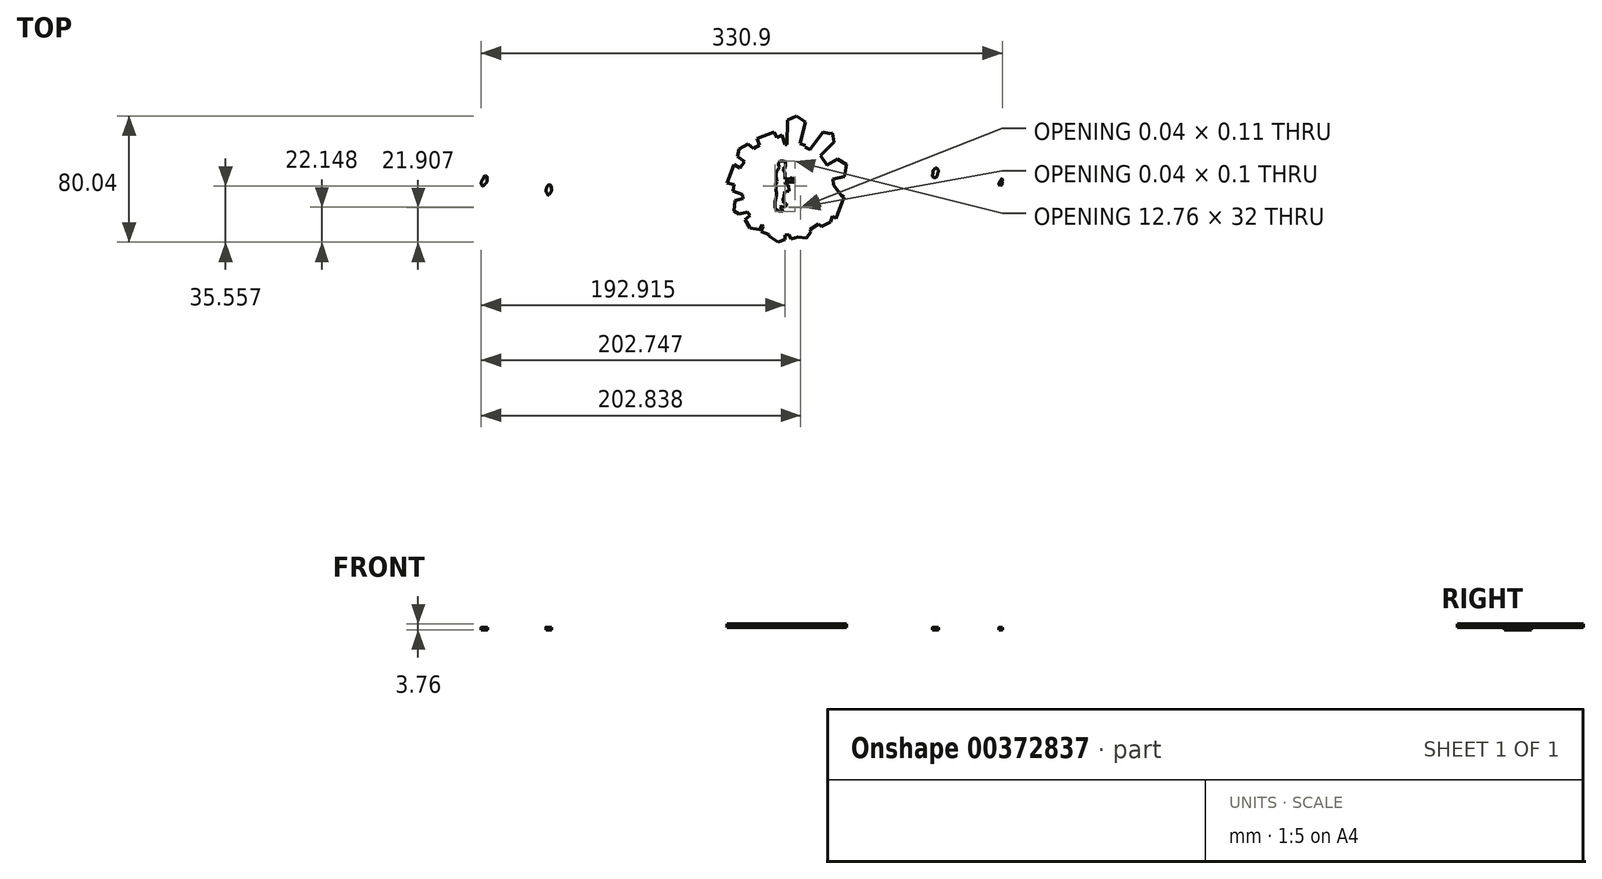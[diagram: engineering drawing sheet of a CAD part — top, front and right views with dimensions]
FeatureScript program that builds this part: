
annotation { "Feature Type Name" : "Feature", "Feature Type Description" : "" }
export const myFeature = defineFeature(function(context is Context, id is Id, definition is map)
    precondition{}
    {
        {
            var Q0;
            Q0=qCreatedBy(makeId("Top.planeOp"),FACE);
            var sketch = newSketch(context, id + "F0", { "sketchPlane" : qUnion([Q0])});
            skFitSpline(sketch, "E0", {"points": [v(-46.5, -16.11) * mm, v(-46.5, -16.11) * mm, v(-56.39, -13.57) * mm, v(-56.67, -12.44) * mm, v(-46.5, -16.11) * mm]});
            skFitSpline(sketch, "E1", {"points": [v(-56.67, -12.44) * mm, v(-56.95, -11.3) * mm, v(-55.82, -5.94) * mm, v(-55.82, -5.94) * mm, v(-56.67, -12.44) * mm]});
            skFitSpline(sketch, "E2", {"points": [v(-55.82, -5.94) * mm, v(-55.82, -5.94) * mm, v(-63.17, -5.09) * mm, v(-63.17, -3.96) * mm, v(-55.82, -5.94) * mm]});
            skFitSpline(sketch, "E3", {"points": [v(-63.17, -3.96) * mm, v(-63.17, -2.83) * mm, v(-55.54, 15.54) * mm, v(-55.54, 15.54) * mm, v(-63.17, -3.96) * mm]});
            skFitSpline(sketch, "E4", {"points": [v(21.34, -62.18) * mm, v(21.34, -62.18) * mm, v(14, -60.48) * mm, v(12.01, -61.33) * mm, v(21.34, -62.18) * mm]});
            skFitSpline(sketch, "E5", {"points": [v(12.01, -61.33) * mm, v(10.03, -62.18) * mm, v(4.66, -63.31) * mm, v(4.66, -63.31) * mm, v(12.01, -61.33) * mm]});
            skLineSegment(sketch, "E6", {"start": v(-55.54, 15.54) * mm, "end": v(-49.32, 11.59) * mm});
            skLineSegment(sketch, "E7", {"start": v(-49.32, 11.59) * mm, "end": v(-44.8, 18.37) * mm});
            skLineSegment(sketch, "E8", {"start": v(-44.8, 18.37) * mm, "end": v(-51.86, 23.74) * mm});
            skLineSegment(sketch, "E9", {"start": v(-51.86, 23.74) * mm, "end": v(-50.17, 31.66) * mm});
            skLineSegment(sketch, "E10", {"start": v(-50.17, 31.66) * mm, "end": v(-40.84, 37.03) * mm});
            skLineSegment(sketch, "E11", {"start": v(-40.84, 37.03) * mm, "end": v(-34.9, 32.5) * mm});
            skLineSegment(sketch, "E12", {"start": v(-34.9, 32.5) * mm, "end": v(-28.4, 36.18) * mm});
            skLineSegment(sketch, "E13", {"start": v(-28.4, 36.18) * mm, "end": v(-31.23, 42.68) * mm});
            skLineSegment(sketch, "E14", {"start": v(-31.23, 42.68) * mm, "end": v(-13.14, 49.74) * mm});
            skLineSegment(sketch, "E15", {"start": v(-13.14, 49.74) * mm, "end": v(-10.03, 43.8) * mm});
            skLineSegment(sketch, "E16", {"start": v(-10.03, 43.8) * mm, "end": v(-4.66, 46.63) * mm});
            skLineSegment(sketch, "E17", {"start": v(-4.66, 46.63) * mm, "end": v(-1.84, 36.74) * mm});
            skLineSegment(sketch, "E18", {"start": v(-1.84, 36.74) * mm, "end": v(0.42, 36.74) * mm});
            skLineSegment(sketch, "E19", {"start": v(0.42, 36.74) * mm, "end": v(0.99, 62.74) * mm});
            skLineSegment(sketch, "E20", {"start": v(0.99, 62.74) * mm, "end": v(10.32, 66.7) * mm});
            skLineSegment(sketch, "E21", {"start": v(10.32, 66.7) * mm, "end": v(20.2, 60.2) * mm});
            skLineSegment(sketch, "E22", {"start": v(20.2, 60.2) * mm, "end": v(14, 37.87) * mm});
            skLineSegment(sketch, "E23", {"start": v(14, 37.87) * mm, "end": v(20.2, 35.61) * mm});
            skLineSegment(sketch, "E24", {"start": v(20.2, 35.61) * mm, "end": v(19.64, 33.92) * mm});
            skLineSegment(sketch, "E25", {"start": v(19.64, 33.92) * mm, "end": v(25.01, 31.37) * mm});
            skLineSegment(sketch, "E26", {"start": v(25.01, 31.37) * mm, "end": v(38.3, 50.03) * mm});
            skLineSegment(sketch, "E27", {"start": v(38.3, 50.03) * mm, "end": v(45.36, 48.05) * mm});
            skLineSegment(sketch, "E28", {"start": v(45.36, 48.05) * mm, "end": v(48.75, 48.9) * mm});
            skLineSegment(sketch, "E29", {"start": v(48.75, 48.9) * mm, "end": v(50.17, 39.29) * mm});
            skLineSegment(sketch, "E30", {"start": v(50.17, 39.29) * mm, "end": v(35.75, 24.87) * mm});
            skLineSegment(sketch, "E31", {"start": v(35.75, 24.87) * mm, "end": v(42.82, 14.98) * mm});
            skLineSegment(sketch, "E32", {"start": v(42.82, 14.98) * mm, "end": v(53.84, 21.48) * mm});
            skLineSegment(sketch, "E33", {"start": v(53.84, 21.48) * mm, "end": v(63.17, 15.54) * mm});
            skLineSegment(sketch, "E34", {"start": v(63.17, 15.54) * mm, "end": v(61.47, 2.54) * mm});
            skLineSegment(sketch, "E35", {"start": v(61.47, 2.54) * mm, "end": v(49.32, 0) * mm});
            skLineSegment(sketch, "E36", {"start": v(49.32, 0) * mm, "end": v(49.89, -6.22) * mm});
            skLineSegment(sketch, "E37", {"start": v(49.89, -6.22) * mm, "end": v(58.36, -17.52) * mm});
            skLineSegment(sketch, "E38", {"start": v(58.36, -17.52) * mm, "end": v(60.9, -19.22) * mm});
            skLineSegment(sketch, "E39", {"start": v(60.9, -19.22) * mm, "end": v(52.15, -41.55) * mm});
            skLineSegment(sketch, "E40", {"start": v(52.15, -41.55) * mm, "end": v(48.47, -39.29) * mm});
            skLineSegment(sketch, "E41", {"start": v(48.47, -39.29) * mm, "end": v(46.5, -45.22) * mm});
            skLineSegment(sketch, "E42", {"start": v(46.5, -45.22) * mm, "end": v(36.88, -50.03) * mm});
            skLineSegment(sketch, "E43", {"start": v(36.88, -50.03) * mm, "end": v(33.77, -47.48) * mm});
            skLineSegment(sketch, "E44", {"start": v(33.77, -47.48) * mm, "end": v(24.73, -53.42) * mm});
            skLineSegment(sketch, "E45", {"start": v(24.73, -53.42) * mm, "end": v(25.58, -55.68) * mm});
            skLineSegment(sketch, "E46", {"start": v(25.58, -55.68) * mm, "end": v(21.34, -62.18) * mm});
            skFitSpline(sketch, "E47", {"points": [v(-7.41, 12.72) * mm, v(-7.66, 13.34) * mm, v(-8.77, 14.69) * mm, v(-8.77, 14.69) * mm, v(-7.41, 12.72) * mm]});
            skFitSpline(sketch, "E48", {"points": [v(-8.77, 14.69) * mm, v(-8.77, 14.69) * mm, v(-8.64, 16.16) * mm, v(-8.64, 16.9) * mm, v(-8.77, 14.69) * mm]});
            skFitSpline(sketch, "E49", {"points": [v(-8.64, 16.9) * mm, v(-8.64, 17.64) * mm, v(-6.8, 19.23) * mm, v(-6.8, 19.23) * mm, v(-8.64, 16.9) * mm]});
            skLineSegment(sketch, "E50", {"start": v(4.66, -63.31) * mm, "end": v(2.69, -58.79) * mm});
            skLineSegment(sketch, "E51", {"start": v(2.69, -58.79) * mm, "end": v(-1.84, -59.07) * mm});
            skLineSegment(sketch, "E52", {"start": v(-1.84, -59.07) * mm, "end": v(-1.84, -64.16) * mm});
            skLineSegment(sketch, "E53", {"start": v(-1.84, -64.16) * mm, "end": v(-9.19, -66.7) * mm});
            skLineSegment(sketch, "E54", {"start": v(-9.19, -66.7) * mm, "end": v(-18.8, -60.48) * mm});
            skLineSegment(sketch, "E55", {"start": v(-18.8, -60.48) * mm, "end": v(-18.51, -58.5) * mm});
            skLineSegment(sketch, "E56", {"start": v(-18.51, -58.5) * mm, "end": v(-27.27, -55.4) * mm});
            skLineSegment(sketch, "E57", {"start": v(-27.27, -55.4) * mm, "end": v(-24.73, -50.3) * mm});
            skLineSegment(sketch, "E58", {"start": v(-24.73, -50.3) * mm, "end": v(-26.14, -48.05) * mm});
            skLineSegment(sketch, "E59", {"start": v(-26.14, -48.05) * mm, "end": v(-28.69, -53.14) * mm});
            skLineSegment(sketch, "E60", {"start": v(-28.69, -53.14) * mm, "end": v(-38.86, -51.72) * mm});
            skLineSegment(sketch, "E61", {"start": v(-38.86, -51.72) * mm, "end": v(-44.23, -42.68) * mm});
            skLineSegment(sketch, "E62", {"start": v(-44.23, -42.68) * mm, "end": v(-38.58, -38.72) * mm});
            skLineSegment(sketch, "E63", {"start": v(-38.58, -38.72) * mm, "end": v(-41.12, -35.05) * mm});
            skLineSegment(sketch, "E64", {"start": v(-41.12, -35.05) * mm, "end": v(-50.45, -37.03) * mm});
            skLineSegment(sketch, "E65", {"start": v(-50.45, -37.03) * mm, "end": v(-55.54, -33.63) * mm});
            skLineSegment(sketch, "E66", {"start": v(-55.54, -33.63) * mm, "end": v(-54.4, -22.61) * mm});
            skLineSegment(sketch, "E67", {"start": v(-54.4, -22.61) * mm, "end": v(-45.93, -20.63) * mm});
            skLineSegment(sketch, "E68", {"start": v(-45.93, -20.63) * mm, "end": v(-46.5, -16.11) * mm});
            skFitSpline(sketch, "E69", {"points": [v(-1.02, 13.95) * mm, v(-1.02, 13.95) * mm, v(-1.76, 13.34) * mm, v(-1.88, 12.6) * mm, v(-1.02, 13.95) * mm]});
            skFitSpline(sketch, "E70", {"points": [v(-1.88, 12.6) * mm, v(-2, 11.86) * mm, v(-1.88, 11.12) * mm, v(-1.88, 11.12) * mm, v(-1.88, 12.6) * mm]});
            skLineSegment(sketch, "E71", {"start": v(-6.8, 19.23) * mm, "end": v(-3.6, 19.11) * mm});
            skLineSegment(sketch, "E72", {"start": v(-3.6, 19.11) * mm, "end": v(-1.27, 18.62) * mm});
            skLineSegment(sketch, "E73", {"start": v(-1.27, 18.62) * mm, "end": v(-1.4, 16.16) * mm});
            skLineSegment(sketch, "E74", {"start": v(-1.4, 16.16) * mm, "end": v(-1.02, 13.95) * mm});
            skFitSpline(sketch, "E75", {"points": [v(-1.76, 6.58) * mm, v(-1.76, 6.58) * mm, v(-2, 4.36) * mm, v(-1.88, 3.87) * mm, v(-1.76, 6.58) * mm]});
            skFitSpline(sketch, "E76", {"points": [v(-1.88, 3.87) * mm, v(-1.76, 3.38) * mm, v(-1.52, 0.3) * mm, v(-1.52, 0.3) * mm, v(-1.88, 3.87) * mm]});
            skLineSegment(sketch, "E77", {"start": v(-1.88, 11.12) * mm, "end": v(-3.36, 11.37) * mm});
            skLineSegment(sketch, "E78", {"start": v(-3.36, 11.37) * mm, "end": v(-4.34, 10.88) * mm});
            skLineSegment(sketch, "E79", {"start": v(-4.34, 10.88) * mm, "end": v(-3.36, 9.4) * mm});
            skLineSegment(sketch, "E80", {"start": v(-3.36, 9.4) * mm, "end": v(-2.5, 8.54) * mm});
            skLineSegment(sketch, "E81", {"start": v(-2.5, 8.54) * mm, "end": v(-1.76, 6.58) * mm});
            skFitSpline(sketch, "E82", {"points": [v(5.74, 2.28) * mm, v(5.74, 2.28) * mm, v(6.84, 1.3) * mm, v(6.47, 0.92) * mm, v(5.74, 2.28) * mm]});
            skFitSpline(sketch, "E83", {"points": [v(6.47, 0.92) * mm, v(6.1, 0.55) * mm, v(5.24, -0.06) * mm, v(5.24, -0.06) * mm, v(6.47, 0.92) * mm]});
            skLineSegment(sketch, "E84", {"start": v(-1.52, 0.3) * mm, "end": v(3.03, -0.06) * mm});
            skLineSegment(sketch, "E85", {"start": v(3.03, -0.06) * mm, "end": v(5.37, 1.54) * mm});
            skLineSegment(sketch, "E86", {"start": v(5.37, 1.54) * mm, "end": v(5.74, 2.28) * mm});
            skFitSpline(sketch, "E87", {"points": [v(-4.46, -34.1) * mm, v(-4.46, -34.1) * mm, v(-6.92, -33.98) * mm, v(-7.54, -33.85) * mm, v(-4.46, -34.1) * mm]});
            skFitSpline(sketch, "E88", {"points": [v(-7.54, -33.85) * mm, v(-8.15, -33.73) * mm, v(-9.5, -33.24) * mm, v(-10, -33) * mm]});
            skFitSpline(sketch, "E89", {"points": [v(-10, -33) * mm, v(-10.49, -32.75) * mm, v(-12.33, -30.66) * mm, v(-12.33, -30.66) * mm, v(-10, -33) * mm]});
            skLineSegment(sketch, "E90", {"start": v(5.24, -0.06) * mm, "end": v(7.58, -0.67) * mm});
            skLineSegment(sketch, "E91", {"start": v(7.58, -0.67) * mm, "end": v(8.93, -1.9) * mm});
            skLineSegment(sketch, "E92", {"start": v(8.93, -1.9) * mm, "end": v(7.82, -2.89) * mm});
            skLineSegment(sketch, "E93", {"start": v(7.82, -2.89) * mm, "end": v(2.3, -3.13) * mm});
            skLineSegment(sketch, "E94", {"start": v(2.3, -3.13) * mm, "end": v(-1.64, -2.89) * mm});
            skLineSegment(sketch, "E95", {"start": v(-1.64, -2.89) * mm, "end": v(-1.27, -5.22) * mm});
            skLineSegment(sketch, "E96", {"start": v(-1.27, -5.22) * mm, "end": v(-0.04, -6.45) * mm});
            skLineSegment(sketch, "E97", {"start": v(-0.04, -6.45) * mm, "end": v(2.17, -6.2) * mm});
            skLineSegment(sketch, "E98", {"start": v(2.17, -6.2) * mm, "end": v(2.42, -12.72) * mm});
            skLineSegment(sketch, "E99", {"start": v(2.42, -12.72) * mm, "end": v(-2, -12.96) * mm});
            skLineSegment(sketch, "E100", {"start": v(-2, -12.96) * mm, "end": v(-2.74, -18.98) * mm});
            skLineSegment(sketch, "E101", {"start": v(-2.74, -18.98) * mm, "end": v(-3.6, -21.32) * mm});
            skLineSegment(sketch, "E102", {"start": v(-3.6, -21.32) * mm, "end": v(-3.36, -25.37) * mm});
            skLineSegment(sketch, "E103", {"start": v(-3.36, -25.37) * mm, "end": v(-0.16, -26.11) * mm});
            skLineSegment(sketch, "E104", {"start": v(-0.16, -26.11) * mm, "end": v(0.08, -28.2) * mm});
            skLineSegment(sketch, "E105", {"start": v(0.08, -28.2) * mm, "end": v(-2, -29.43) * mm});
            skLineSegment(sketch, "E106", {"start": v(-2, -29.43) * mm, "end": v(-5.57, -29.3) * mm});
            skLineSegment(sketch, "E107", {"start": v(-5.57, -29.3) * mm, "end": v(-6.92, -29.68) * mm});
            skLineSegment(sketch, "E108", {"start": v(-6.92, -29.68) * mm, "end": v(-4.96, -31.89) * mm});
            skLineSegment(sketch, "E109", {"start": v(-4.96, -31.89) * mm, "end": v(-4.46, -34.1) * mm});
            skFitSpline(sketch, "E110", {"points": [v(-12.33, -24.15) * mm, v(-12.33, -24.15) * mm, v(-11.22, -20.1) * mm, v(-11.1, -19.35) * mm, v(-12.33, -24.15) * mm]});
            skFitSpline(sketch, "E111", {"points": [v(-11.1, -19.35) * mm, v(-10.98, -18.62) * mm, v(-10.6, -15.05) * mm, v(-10.73, -14.44) * mm]});
            skFitSpline(sketch, "E112", {"points": [v(-10.73, -14.44) * mm, v(-10.85, -13.82) * mm, v(-11.22, -10.87) * mm, v(-11.35, -10.14) * mm]});
            skFitSpline(sketch, "E113", {"points": [v(-11.35, -10.14) * mm, v(-11.47, -9.4) * mm, v(-11.47, -5.34) * mm, v(-11.47, -5.34) * mm, v(-11.35, -10.14) * mm]});
            skFitSpline(sketch, "E114", {"points": [v(-11.47, -5.34) * mm, v(-11.47, -5.34) * mm, v(-10.49, -3.13) * mm, v(-10.36, -2.64) * mm, v(-11.47, -5.34) * mm]});
            skFitSpline(sketch, "E115", {"points": [v(-10.36, -2.64) * mm, v(-10.24, -2.15) * mm, v(-10.6, -0.06) * mm, v(-10.6, -0.06) * mm, v(-10.36, -2.64) * mm]});
            skFitSpline(sketch, "E116", {"points": [v(-10.6, -0.06) * mm, v(-10.6, -0.06) * mm, v(-11.3, 3.5) * mm, v(-11.22, 4.12) * mm, v(-10.6, -0.06) * mm]});
            skLineSegment(sketch, "E117", {"start": v(-12.33, -30.66) * mm, "end": v(-12.33, -24.15) * mm});
            skLineSegment(sketch, "E118", {"start": v(-12.33, -24.15) * mm, "end": v(-12.33, -30.66) * mm});
            skLineSegment(sketch, "E119", {"start": v(-11.22, 4.12) * mm, "end": v(-10.73, 8.17) * mm});
            skLineSegment(sketch, "E120", {"start": v(-10.73, 8.17) * mm, "end": v(-9.26, 9.9) * mm});
            skLineSegment(sketch, "E121", {"start": v(-9.26, 9.9) * mm, "end": v(-8.4, 11.25) * mm});
            skLineSegment(sketch, "E122", {"start": v(-8.4, 11.25) * mm, "end": v(-7.41, 12.72) * mm});
            skFitSpline(sketch, "E123", {"points": [v(19.38, 11.86) * mm, v(19.38, 11.86) * mm, v(19.25, 12.72) * mm, v(19.25, 13.21) * mm, v(19.38, 11.86) * mm]});
            skFitSpline(sketch, "E124", {"points": [v(19.25, 13.21) * mm, v(19.25, 13.7) * mm, v(19.25, 14.32) * mm, v(19.13, 14.8) * mm]});
            skFitSpline(sketch, "E125", {"points": [v(19.13, 14.8) * mm, v(19, 15.3) * mm, v(18.64, 15.42) * mm, v(18.64, 16.04) * mm]});
            skFitSpline(sketch, "E126", {"points": [v(18.64, 16.04) * mm, v(18.64, 16.65) * mm, v(20.48, 17.76) * mm, v(20.48, 17.76) * mm, v(18.64, 16.04) * mm]});
            skLineSegment(sketch, "E127", {"start": v(22.08, 9.03) * mm, "end": v(20.36, 10.63) * mm});
            skLineSegment(sketch, "E128", {"start": v(20.36, 10.63) * mm, "end": v(19.38, 11.86) * mm});
            skFitSpline(sketch, "E129", {"points": [v(23.06, 18.62) * mm, v(23.06, 18.62) * mm, v(24.05, 18.13) * mm, v(24.41, 18.13) * mm, v(23.06, 18.62) * mm]});
            skFitSpline(sketch, "E130", {"points": [v(24.41, 18.13) * mm, v(24.78, 18.13) * mm, v(25.52, 17.27) * mm, v(25.52, 17.27) * mm, v(24.41, 18.13) * mm]});
            skLineSegment(sketch, "E131", {"start": v(20.48, 17.76) * mm, "end": v(21.34, 18.37) * mm});
            skLineSegment(sketch, "E132", {"start": v(21.34, 18.37) * mm, "end": v(23.06, 18.62) * mm});
            skFitSpline(sketch, "E133", {"points": [v(26.01, 16.28) * mm, v(26.01, 16.28) * mm, v(25.89, 15.92) * mm, v(25.89, 15.3) * mm, v(26.01, 16.28) * mm]});
            skLineSegment(sketch, "E134", {"start": v(25.52, 17.27) * mm, "end": v(26.01, 16.28) * mm});
            skFitSpline(sketch, "E135", {"points": [v(28.35, 9.53) * mm, v(28.35, 9.53) * mm, v(28.84, 8.91) * mm, v(29.2, 8.42) * mm, v(28.35, 9.53) * mm]});
            skFitSpline(sketch, "E136", {"points": [v(29.2, 8.42) * mm, v(29.58, 7.93) * mm, v(30.19, 8.17) * mm, v(30.19, 7.2) * mm]});
            skFitSpline(sketch, "E137", {"points": [v(30.19, 7.2) * mm, v(30.19, 6.2) * mm, v(29.94, 5.22) * mm, v(29.94, 4.49) * mm]});
            skFitSpline(sketch, "E138", {"points": [v(29.94, 4.49) * mm, v(29.94, 3.75) * mm, v(30.19, 3.01) * mm, v(30.19, 2.4) * mm]});
            skFitSpline(sketch, "E139", {"points": [v(30.19, 2.4) * mm, v(30.19, 1.78) * mm, v(29.45, 0.06) * mm, v(29.7, -1.04) * mm]});
            skFitSpline(sketch, "E140", {"points": [v(29.7, -1.04) * mm, v(29.94, -2.15) * mm, v(29.94, -2.4) * mm, v(30.07, -2.76) * mm]});
            skFitSpline(sketch, "E141", {"points": [v(30.07, -2.76) * mm, v(30.19, -3.13) * mm, v(30.56, -4.6) * mm, v(30.56, -5.1) * mm]});
            skFitSpline(sketch, "E142", {"points": [v(30.56, -5.1) * mm, v(30.56, -5.59) * mm, v(30.44, -6.57) * mm, v(29.82, -7.43) * mm]});
            skFitSpline(sketch, "E143", {"points": [v(29.82, -7.43) * mm, v(29.2, -8.3) * mm, v(29.08, -7.8) * mm, v(29.08, -8.54) * mm]});
            skFitSpline(sketch, "E144", {"points": [v(29.08, -8.54) * mm, v(29.08, -9.28) * mm, v(28.96, -8.78) * mm, v(29.08, -9.77) * mm]});
            skFitSpline(sketch, "E145", {"points": [v(29.08, -9.77) * mm, v(29.2, -10.75) * mm, v(29.2, -11.12) * mm, v(29.2, -11.73) * mm]});
            skFitSpline(sketch, "E146", {"points": [v(29.2, -11.73) * mm, v(29.2, -12.35) * mm, v(29.33, -13.7) * mm, v(29.33, -13.7) * mm, v(29.2, -11.73) * mm]});
            skLineSegment(sketch, "E147", {"start": v(25.89, 15.3) * mm, "end": v(25.89, 13.95) * mm});
            skLineSegment(sketch, "E148", {"start": v(25.89, 13.95) * mm, "end": v(25.64, 13.21) * mm});
            skLineSegment(sketch, "E149", {"start": v(25.64, 13.21) * mm, "end": v(25.52, 12.23) * mm});
            skLineSegment(sketch, "E150", {"start": v(25.52, 12.23) * mm, "end": v(26.01, 11.25) * mm});
            skLineSegment(sketch, "E151", {"start": v(26.01, 11.25) * mm, "end": v(28.35, 9.53) * mm});
            skFitSpline(sketch, "E152", {"points": [v(23.8, -35.33) * mm, v(23.8, -35.33) * mm, v(23.19, -35.08) * mm, v(22.7, -35.08) * mm, v(23.8, -35.33) * mm]});
            skFitSpline(sketch, "E153", {"points": [v(22.7, -35.08) * mm, v(22.2, -35.08) * mm, v(21.71, -34.84) * mm, v(21.71, -34.84) * mm, v(22.7, -35.08) * mm]});
            skLineSegment(sketch, "E154", {"start": v(29.33, -13.7) * mm, "end": v(34.61, -13.7) * mm});
            skLineSegment(sketch, "E155", {"start": v(34.61, -13.7) * mm, "end": v(35.1, -24.27) * mm});
            skLineSegment(sketch, "E156", {"start": v(35.1, -24.27) * mm, "end": v(28.96, -25.13) * mm});
            skLineSegment(sketch, "E157", {"start": v(28.96, -25.13) * mm, "end": v(29.33, -28.82) * mm});
            skLineSegment(sketch, "E158", {"start": v(29.33, -28.82) * mm, "end": v(29.33, -31.64) * mm});
            skLineSegment(sketch, "E159", {"start": v(29.33, -31.64) * mm, "end": v(29.33, -33.49) * mm});
            skLineSegment(sketch, "E160", {"start": v(29.33, -33.49) * mm, "end": v(27.13, -34.53) * mm});
            skLineSegment(sketch, "E161", {"start": v(27.13, -34.53) * mm, "end": v(25.52, -35.2) * mm});
            skLineSegment(sketch, "E162", {"start": v(25.52, -35.2) * mm, "end": v(23.8, -35.33) * mm});
            skFitSpline(sketch, "E163", {"points": [v(21.71, -34.22) * mm, v(21.71, -34.22) * mm, v(21.34, -34.35) * mm, v(21.83, -33.73) * mm, v(21.71, -34.22) * mm]});
            skFitSpline(sketch, "E164", {"points": [v(21.83, -33.73) * mm, v(22.32, -33.12) * mm, v(22.45, -33.12) * mm, v(22.45, -33.12) * mm, v(21.83, -33.73) * mm]});
            skLineSegment(sketch, "E165", {"start": v(21.71, -34.84) * mm, "end": v(21.71, -34.22) * mm});
            skFitSpline(sketch, "E166", {"points": [v(24.3, -32.26) * mm, v(24.66, -32.01) * mm, v(24.78, -31.76) * mm, v(24.78, -31.76) * mm, v(24.3, -32.26) * mm]});
            skLineSegment(sketch, "E167", {"start": v(22.45, -33.12) * mm, "end": v(23.92, -32.5) * mm});
            skLineSegment(sketch, "E168", {"start": v(23.92, -32.5) * mm, "end": v(24.3, -32.26) * mm});
            skFitSpline(sketch, "E169", {"points": [v(24.3, -29.92) * mm, v(24.3, -29.92) * mm, v(24.41, -30.29) * mm, v(24.17, -29.8) * mm, v(24.3, -29.92) * mm]});
            skFitSpline(sketch, "E170", {"points": [v(24.17, -29.8) * mm, v(23.92, -29.3) * mm, v(23.68, -28.57) * mm, v(23.68, -28.57) * mm, v(24.17, -29.8) * mm]});
            skFitSpline(sketch, "E171", {"points": [v(23.68, -28.57) * mm, v(23.68, -28.57) * mm, v(23.55, -28.57) * mm, v(23.43, -29.18) * mm, v(23.68, -28.57) * mm]});
            skFitSpline(sketch, "E172", {"points": [v(23.43, -29.18) * mm, v(23.3, -29.8) * mm, v(22.7, -30.84) * mm, v(22.7, -30.84) * mm, v(23.43, -29.18) * mm]});
            skLineSegment(sketch, "E173", {"start": v(24.78, -31.76) * mm, "end": v(24.78, -31.03) * mm});
            skLineSegment(sketch, "E174", {"start": v(24.78, -31.03) * mm, "end": v(24.3, -29.92) * mm});
            skFitSpline(sketch, "E175", {"points": [v(22.94, -30.66) * mm, v(22.94, -30.66) * mm, v(22.45, -30.84) * mm, v(21.83, -30.72) * mm, v(22.94, -30.66) * mm]});
            skFitSpline(sketch, "E176", {"points": [v(21.83, -30.72) * mm, v(21.22, -30.6) * mm, v(21.59, -30.72) * mm, v(20.85, -30.6) * mm]});
            skFitSpline(sketch, "E177", {"points": [v(20.85, -30.6) * mm, v(20.11, -30.47) * mm, v(21.1, -30.47) * mm, v(20, -30.47) * mm]});
            skFitSpline(sketch, "E178", {"points": [v(20, -30.47) * mm, v(18.88, -30.47) * mm, v(19.87, -30.35) * mm, v(18.88, -30.47) * mm]});
            skFitSpline(sketch, "E179", {"points": [v(18.88, -30.47) * mm, v(17.9, -30.6) * mm, v(17.78, -30.6) * mm, v(17.78, -30.6) * mm, v(18.88, -30.47) * mm]});
            skFitSpline(sketch, "E180", {"points": [v(17.78, -30.6) * mm, v(17.78, -30.6) * mm, v(17.78, -30.72) * mm, v(17.04, -30.47) * mm, v(17.78, -30.6) * mm]});
            skFitSpline(sketch, "E181", {"points": [v(17.04, -30.47) * mm, v(16.3, -30.23) * mm, v(16.92, -30.66) * mm, v(15.93, -30.54) * mm]});
            skFitSpline(sketch, "E182", {"points": [v(15.93, -30.54) * mm, v(14.95, -30.41) * mm, v(15.2, -30.23) * mm, v(14.7, -29.86) * mm]});
            skFitSpline(sketch, "E183", {"points": [v(14.7, -29.86) * mm, v(14.66, -29.7) * mm, v(14.87, -30.27) * mm, v(14.83, -30.1) * mm]});
            skFitSpline(sketch, "E184", {"points": [v(14.83, -30.1) * mm, v(12.95, -28.8) * mm, v(16.5, -27.6) * mm, v(17.35, -27.34) * mm]});
            skFitSpline(sketch, "E185", {"points": [v(17.35, -27.34) * mm, v(18.95, -26.85) * mm, v(19.25, -26.91) * mm, v(19.25, -26.91) * mm, v(17.35, -27.34) * mm]});
            skLineSegment(sketch, "E186", {"start": v(22.7, -30.84) * mm, "end": v(22.94, -30.66) * mm});
            skFitSpline(sketch, "E187", {"points": [v(20.11, -11.98) * mm, v(20.11, -11) * mm, v(20.24, -10.26) * mm, v(20, -9.52) * mm]});
            skFitSpline(sketch, "E188", {"points": [v(20, -9.52) * mm, v(19.74, -8.78) * mm, v(19.5, -7.92) * mm, v(19.87, -6.82) * mm]});
            skFitSpline(sketch, "E189", {"points": [v(19.87, -6.82) * mm, v(20.24, -5.71) * mm, v(20.11, -2.89) * mm, v(20.11, -2.89) * mm, v(19.87, -6.82) * mm]});
            skLineSegment(sketch, "E190", {"start": v(19.25, -26.91) * mm, "end": v(20, -26.3) * mm});
            skLineSegment(sketch, "E191", {"start": v(20, -26.3) * mm, "end": v(20.24, -24.51) * mm});
            skLineSegment(sketch, "E192", {"start": v(20.24, -24.51) * mm, "end": v(20.11, -18.25) * mm});
            skLineSegment(sketch, "E193", {"start": v(20.11, -18.25) * mm, "end": v(20.11, -15.05) * mm});
            skLineSegment(sketch, "E194", {"start": v(20.11, -15.05) * mm, "end": v(20.11, -11.98) * mm});
            skFitSpline(sketch, "E195", {"points": [v(19.38, -1.78) * mm, v(19.38, -1.78) * mm, v(18.64, -2.4) * mm, v(17.4, -3.13) * mm, v(19.38, -1.78) * mm]});
            skFitSpline(sketch, "E196", {"points": [v(17.4, -3.13) * mm, v(16.18, -3.87) * mm, v(15.57, -4.11) * mm, v(15.57, -4.11) * mm, v(17.4, -3.13) * mm]});
            skLineSegment(sketch, "E197", {"start": v(20.11, -2.89) * mm, "end": v(19.38, -1.78) * mm});
            skFitSpline(sketch, "E198", {"points": [v(15.07, -3.62) * mm, v(15.07, -3.62) * mm, v(15.57, -3.38) * mm, v(14.46, -3.38) * mm, v(15.07, -3.62) * mm]});
            skLineSegment(sketch, "E199", {"start": v(15.57, -4.11) * mm, "end": v(15.07, -3.62) * mm});
            skLineSegment(sketch, "E200", {"start": v(14.46, -3.38) * mm, "end": v(12.99, -3.38) * mm});
            skLineSegment(sketch, "E201", {"start": v(12.99, -3.38) * mm, "end": v(11.51, -3.38) * mm});
            skLineSegment(sketch, "E202", {"start": v(11.51, -3.38) * mm, "end": v(10.53, -2.89) * mm});
            skLineSegment(sketch, "E203", {"start": v(10.53, -2.89) * mm, "end": v(12, -1.66) * mm});
            skLineSegment(sketch, "E204", {"start": v(12, -1.66) * mm, "end": v(12.62, -1.17) * mm});
            skLineSegment(sketch, "E205", {"start": v(12.62, -1.17) * mm, "end": v(12.99, -0.92) * mm});
            skLineSegment(sketch, "E206", {"start": v(12.99, -0.92) * mm, "end": v(12.62, 0.19) * mm});
            skLineSegment(sketch, "E207", {"start": v(12.62, 0.19) * mm, "end": v(13.1, 0.55) * mm});
            skLineSegment(sketch, "E208", {"start": v(13.1, 0.55) * mm, "end": v(13.6, 0.55) * mm});
            skFitSpline(sketch, "E209", {"points": [v(20.6, 7.31) * mm, v(20.6, 7.31) * mm, v(20.24, 6.33) * mm, v(20.24, 5.72) * mm, v(20.6, 7.31) * mm]});
            skFitSpline(sketch, "E210", {"points": [v(20.24, 5.72) * mm, v(20.24, 5.1) * mm, v(20.11, 4) * mm, v(20.11, 4) * mm, v(20.24, 5.72) * mm]});
            skLineSegment(sketch, "E211", {"start": v(21.96, 9.53) * mm, "end": v(20.6, 7.31) * mm});
            skLineSegment(sketch, "E212", {"start": v(20.11, 4) * mm, "end": v(19.74, 1.9) * mm});
            skLineSegment(sketch, "E213", {"start": v(19.74, 1.9) * mm, "end": v(19.25, 1.42) * mm});
            skLineSegment(sketch, "E214", {"start": v(19.25, 1.42) * mm, "end": v(17.78, 0.43) * mm});
            skLineSegment(sketch, "E215", {"start": v(17.78, 0.43) * mm, "end": v(15.32, -0.3) * mm});
            skLineSegment(sketch, "E216", {"start": v(15.32, -0.3) * mm, "end": v(13.35, 0.43) * mm});
            skLineSegment(sketch, "E217", {"start": v(13.35, 0.43) * mm, "end": v(13.1, 0.55) * mm});
            skSolve(sketch);
        }
        {
            var Q0;
            Q0=qCreatedBy(makeId("Top.planeOp"),FACE);
            var sketch = newSketch(context, id + "F1", { "sketchPlane" : qUnion([Q0])});
            skLineSegment(sketch, "E218.0.0", {"start": v(20.36, 10.63) * mm, "end": v(21.8, 9.28) * mm});
            skLineSegment(sketch, "E218.0.1", {"start": v(21.8, 9.28) * mm, "end": v(20.6, 7.31) * mm});
            skLineSegment(sketch, "E218.0.2", {"start": v(20.6, 7.31) * mm, "end": v(20.24, 5.72) * mm});
            skLineSegment(sketch, "E218.0.3", {"start": v(20.24, 5.72) * mm, "end": v(20.11, 4) * mm});
            skLineSegment(sketch, "E218.0.4", {"start": v(20.11, 4) * mm, "end": v(19.74, 1.9) * mm});
            skLineSegment(sketch, "E218.0.5", {"start": v(19.74, 1.9) * mm, "end": v(19.25, 1.42) * mm});
            skLineSegment(sketch, "E218.0.6", {"start": v(19.25, 1.42) * mm, "end": v(17.78, 0.43) * mm});
            skLineSegment(sketch, "E218.0.7", {"start": v(17.78, 0.43) * mm, "end": v(15.32, -0.3) * mm});
            skLineSegment(sketch, "E218.0.8", {"start": v(15.32, -0.3) * mm, "end": v(13.35, 0.43) * mm});
            skLineSegment(sketch, "E218.0.9", {"start": v(13.35, 0.43) * mm, "end": v(13.1, 0.55) * mm});
            skLineSegment(sketch, "E218.0.10", {"start": v(13.1, 0.55) * mm, "end": v(12.62, 0.19) * mm});
            skLineSegment(sketch, "E218.0.11", {"start": v(12.62, 0.19) * mm, "end": v(12.99, -0.92) * mm});
            skLineSegment(sketch, "E218.0.12", {"start": v(12.99, -0.92) * mm, "end": v(12.62, -1.17) * mm});
            skLineSegment(sketch, "E218.0.13", {"start": v(12.62, -1.17) * mm, "end": v(12, -1.66) * mm});
            skLineSegment(sketch, "E218.0.14", {"start": v(12, -1.66) * mm, "end": v(10.53, -2.89) * mm});
            skLineSegment(sketch, "E218.0.15", {"start": v(10.53, -2.89) * mm, "end": v(11.51, -3.38) * mm});
            skLineSegment(sketch, "E218.0.16", {"start": v(11.51, -3.38) * mm, "end": v(12.99, -3.38) * mm});
            skLineSegment(sketch, "E218.0.17", {"start": v(12.99, -3.38) * mm, "end": v(14.46, -3.38) * mm});
            skLineSegment(sketch, "E218.0.18", {"start": v(14.46, -3.38) * mm, "end": v(15.07, -3.62) * mm});
            skLineSegment(sketch, "E218.0.19", {"start": v(15.07, -3.62) * mm, "end": v(15.57, -4.11) * mm});
            skLineSegment(sketch, "E218.0.20", {"start": v(15.57, -4.11) * mm, "end": v(17.4, -3.13) * mm});
            skLineSegment(sketch, "E218.0.21", {"start": v(17.4, -3.13) * mm, "end": v(19.38, -1.78) * mm});
            skLineSegment(sketch, "E218.0.22", {"start": v(19.38, -1.78) * mm, "end": v(20.11, -2.89) * mm});
            skLineSegment(sketch, "E218.0.23", {"start": v(20.11, -2.89) * mm, "end": v(19.87, -6.82) * mm});
            skFitSpline(sketch, "E218.0.24", {"points": [v(19.87, -6.82) * mm, v(19.5, -7.92) * mm, v(19.74, -8.78) * mm, v(20, -9.52) * mm]});
            skFitSpline(sketch, "E218.0.25", {"points": [v(20, -9.52) * mm, v(20.24, -10.26) * mm, v(20.11, -11) * mm, v(20.11, -11.98) * mm]});
            skLineSegment(sketch, "E218.0.26", {"start": v(20.11, -11.98) * mm, "end": v(20.11, -15.05) * mm});
            skLineSegment(sketch, "E218.0.27", {"start": v(20.11, -15.05) * mm, "end": v(20.11, -18.25) * mm});
            skLineSegment(sketch, "E218.0.28", {"start": v(20.11, -18.25) * mm, "end": v(20.24, -24.51) * mm});
            skLineSegment(sketch, "E218.0.29", {"start": v(20.24, -24.51) * mm, "end": v(20, -26.3) * mm});
            skLineSegment(sketch, "E218.0.30", {"start": v(20, -26.3) * mm, "end": v(19.25, -26.91) * mm});
            skLineSegment(sketch, "E218.0.31", {"start": v(19.25, -26.91) * mm, "end": v(17.35, -27.34) * mm});
            skFitSpline(sketch, "E218.0.32", {"points": [v(17.35, -27.34) * mm, v(16.5, -27.6) * mm, v(12.95, -28.8) * mm, v(14.83, -30.1) * mm]});
            skFitSpline(sketch, "E218.0.33", {"points": [v(14.83, -30.1) * mm, v(14.87, -30.27) * mm, v(14.66, -29.7) * mm, v(14.7, -29.86) * mm]});
            skFitSpline(sketch, "E218.0.34", {"points": [v(15.93, -30.54) * mm, v(14.95, -30.41) * mm, v(15.2, -30.23) * mm, v(14.7, -29.86) * mm]});
            skFitSpline(sketch, "E218.0.35", {"points": [v(14.7, -29.86) * mm, v(14.66, -29.7) * mm, v(14.87, -30.27) * mm, v(14.83, -30.1) * mm]});
            skFitSpline(sketch, "E218.0.36", {"points": [v(14.7, -29.86) * mm, v(15.2, -30.23) * mm, v(14.95, -30.41) * mm, v(15.93, -30.54) * mm]});
            skFitSpline(sketch, "E218.0.37", {"points": [v(15.93, -30.54) * mm, v(16.92, -30.66) * mm, v(16.3, -30.23) * mm, v(17.04, -30.47) * mm]});
            skLineSegment(sketch, "E218.0.38", {"start": v(17.04, -30.47) * mm, "end": v(17.78, -30.6) * mm});
            skLineSegment(sketch, "E218.0.39", {"start": v(17.78, -30.6) * mm, "end": v(18.88, -30.47) * mm});
            skFitSpline(sketch, "E218.0.40", {"points": [v(18.88, -30.47) * mm, v(19.87, -30.35) * mm, v(18.88, -30.47) * mm, v(20, -30.47) * mm]});
            skFitSpline(sketch, "E218.0.41", {"points": [v(20, -30.47) * mm, v(21.1, -30.47) * mm, v(20.11, -30.47) * mm, v(20.85, -30.6) * mm]});
            skFitSpline(sketch, "E218.0.42", {"points": [v(20.85, -30.6) * mm, v(21.59, -30.72) * mm, v(21.22, -30.6) * mm, v(21.83, -30.72) * mm]});
            skLineSegment(sketch, "E218.0.43", {"start": v(21.83, -30.72) * mm, "end": v(22.77, -30.67) * mm});
            skLineSegment(sketch, "E218.0.44", {"start": v(22.77, -30.67) * mm, "end": v(23.43, -29.18) * mm});
            skLineSegment(sketch, "E218.0.45", {"start": v(23.43, -29.18) * mm, "end": v(23.68, -28.57) * mm});
            skLineSegment(sketch, "E218.0.46", {"start": v(23.68, -28.57) * mm, "end": v(24.17, -29.8) * mm});
            skLineSegment(sketch, "E218.0.47", {"start": v(24.17, -29.8) * mm, "end": v(24.3, -29.92) * mm});
            skLineSegment(sketch, "E218.0.48", {"start": v(24.3, -29.92) * mm, "end": v(24.78, -31.03) * mm});
            skLineSegment(sketch, "E218.0.49", {"start": v(24.78, -31.03) * mm, "end": v(24.78, -31.76) * mm});
            skLineSegment(sketch, "E218.0.50", {"start": v(24.78, -31.76) * mm, "end": v(24.3, -32.26) * mm});
            skLineSegment(sketch, "E218.0.51", {"start": v(24.3, -32.26) * mm, "end": v(23.92, -32.5) * mm});
            skLineSegment(sketch, "E218.0.52", {"start": v(23.92, -32.5) * mm, "end": v(22.45, -33.12) * mm});
            skLineSegment(sketch, "E218.0.53", {"start": v(22.45, -33.12) * mm, "end": v(21.83, -33.73) * mm});
            skLineSegment(sketch, "E218.0.54", {"start": v(21.83, -33.73) * mm, "end": v(21.71, -34.22) * mm});
            skLineSegment(sketch, "E218.0.55", {"start": v(21.71, -34.22) * mm, "end": v(21.71, -34.84) * mm});
            skLineSegment(sketch, "E218.0.56", {"start": v(21.71, -34.84) * mm, "end": v(22.7, -35.08) * mm});
            skLineSegment(sketch, "E218.0.57", {"start": v(22.7, -35.08) * mm, "end": v(23.8, -35.33) * mm});
            skLineSegment(sketch, "E218.0.58", {"start": v(23.8, -35.33) * mm, "end": v(25.52, -35.2) * mm});
            skLineSegment(sketch, "E218.0.59", {"start": v(25.52, -35.2) * mm, "end": v(27.13, -34.53) * mm});
            skLineSegment(sketch, "E218.0.60", {"start": v(27.13, -34.53) * mm, "end": v(29.33, -33.49) * mm});
            skLineSegment(sketch, "E218.0.61", {"start": v(29.33, -33.49) * mm, "end": v(29.33, -31.64) * mm});
            skLineSegment(sketch, "E218.0.62", {"start": v(29.33, -31.64) * mm, "end": v(29.33, -28.82) * mm});
            skLineSegment(sketch, "E218.0.63", {"start": v(29.33, -28.82) * mm, "end": v(28.96, -25.13) * mm});
            skLineSegment(sketch, "E218.0.64", {"start": v(28.96, -25.13) * mm, "end": v(35.1, -24.27) * mm});
            skLineSegment(sketch, "E218.0.65", {"start": v(35.1, -24.27) * mm, "end": v(34.61, -13.7) * mm});
            skLineSegment(sketch, "E218.0.66", {"start": v(34.61, -13.7) * mm, "end": v(29.33, -13.7) * mm});
            skLineSegment(sketch, "E218.0.67", {"start": v(29.33, -13.7) * mm, "end": v(29.2, -11.73) * mm});
            skFitSpline(sketch, "E218.0.68", {"points": [v(29.2, -11.73) * mm, v(29.2, -11.12) * mm, v(29.2, -10.75) * mm, v(29.08, -9.77) * mm]});
            skFitSpline(sketch, "E218.0.69", {"points": [v(29.08, -9.77) * mm, v(28.96, -8.78) * mm, v(29.08, -9.28) * mm, v(29.08, -8.54) * mm]});
            skFitSpline(sketch, "E218.0.70", {"points": [v(29.08, -8.54) * mm, v(29.08, -7.8) * mm, v(29.2, -8.3) * mm, v(29.82, -7.43) * mm]});
            skFitSpline(sketch, "E218.0.71", {"points": [v(29.82, -7.43) * mm, v(30.44, -6.57) * mm, v(30.56, -5.59) * mm, v(30.56, -5.1) * mm]});
            skFitSpline(sketch, "E218.0.72", {"points": [v(30.56, -5.1) * mm, v(30.56, -4.6) * mm, v(30.19, -3.13) * mm, v(30.07, -2.76) * mm]});
            skFitSpline(sketch, "E218.0.73", {"points": [v(30.07, -2.76) * mm, v(29.94, -2.4) * mm, v(29.94, -2.15) * mm, v(29.7, -1.04) * mm]});
            skFitSpline(sketch, "E218.0.74", {"points": [v(29.7, -1.04) * mm, v(29.45, 0.06) * mm, v(30.19, 1.78) * mm, v(30.19, 2.4) * mm]});
            skFitSpline(sketch, "E218.0.75", {"points": [v(30.19, 2.4) * mm, v(30.19, 3.01) * mm, v(29.94, 3.75) * mm, v(29.94, 4.49) * mm]});
            skFitSpline(sketch, "E218.0.76", {"points": [v(29.94, 4.49) * mm, v(29.94, 5.22) * mm, v(30.19, 6.2) * mm, v(30.19, 7.2) * mm]});
            skFitSpline(sketch, "E218.0.77", {"points": [v(30.19, 7.2) * mm, v(30.19, 8.17) * mm, v(29.58, 7.93) * mm, v(29.2, 8.42) * mm]});
            skLineSegment(sketch, "E218.0.78", {"start": v(29.2, 8.42) * mm, "end": v(28.35, 9.53) * mm});
            skLineSegment(sketch, "E218.0.79", {"start": v(28.35, 9.53) * mm, "end": v(26.01, 11.25) * mm});
            skLineSegment(sketch, "E218.0.80", {"start": v(26.01, 11.25) * mm, "end": v(25.52, 12.23) * mm});
            skLineSegment(sketch, "E218.0.81", {"start": v(25.52, 12.23) * mm, "end": v(25.64, 13.21) * mm});
            skLineSegment(sketch, "E218.0.82", {"start": v(25.64, 13.21) * mm, "end": v(25.89, 13.95) * mm});
            skLineSegment(sketch, "E218.0.83", {"start": v(25.89, 13.95) * mm, "end": v(25.89, 15.3) * mm});
            skLineSegment(sketch, "E218.0.84", {"start": v(25.89, 15.3) * mm, "end": v(26.01, 16.28) * mm});
            skLineSegment(sketch, "E218.0.85", {"start": v(26.01, 16.28) * mm, "end": v(25.52, 17.27) * mm});
            skLineSegment(sketch, "E218.0.86", {"start": v(25.52, 17.27) * mm, "end": v(24.41, 18.13) * mm});
            skLineSegment(sketch, "E218.0.87", {"start": v(24.41, 18.13) * mm, "end": v(23.06, 18.62) * mm});
            skLineSegment(sketch, "E218.0.88", {"start": v(23.06, 18.62) * mm, "end": v(21.34, 18.37) * mm});
            skLineSegment(sketch, "E218.0.89", {"start": v(21.34, 18.37) * mm, "end": v(20.48, 17.76) * mm});
            skLineSegment(sketch, "E218.0.90", {"start": v(20.48, 17.76) * mm, "end": v(18.64, 16.04) * mm});
            skFitSpline(sketch, "E218.0.91", {"points": [v(18.64, 16.04) * mm, v(18.64, 15.42) * mm, v(19, 15.3) * mm, v(19.13, 14.8) * mm]});
            skFitSpline(sketch, "E218.0.92", {"points": [v(19.13, 14.8) * mm, v(19.25, 14.32) * mm, v(19.25, 13.7) * mm, v(19.25, 13.21) * mm]});
            skLineSegment(sketch, "E218.0.93", {"start": v(19.25, 13.21) * mm, "end": v(19.38, 11.86) * mm});
            skLineSegment(sketch, "E218.0.94", {"start": v(19.38, 11.86) * mm, "end": v(20.36, 10.63) * mm});
            skLineSegment(sketch, "E218.1.0", {"start": v(-10.6, -0.06) * mm, "end": v(-10.36, -2.64) * mm});
            skLineSegment(sketch, "E218.1.1", {"start": v(-10.36, -2.64) * mm, "end": v(-11.47, -5.34) * mm});
            skLineSegment(sketch, "E218.1.2", {"start": v(-11.47, -5.34) * mm, "end": v(-11.35, -10.14) * mm});
            skFitSpline(sketch, "E218.1.3", {"points": [v(-11.35, -10.14) * mm, v(-11.22, -10.87) * mm, v(-10.85, -13.82) * mm, v(-10.73, -14.44) * mm]});
            skFitSpline(sketch, "E218.1.4", {"points": [v(-10.73, -14.44) * mm, v(-10.6, -15.05) * mm, v(-10.98, -18.62) * mm, v(-11.1, -19.35) * mm]});
            skLineSegment(sketch, "E218.1.5", {"start": v(-11.1, -19.35) * mm, "end": v(-12.33, -24.15) * mm});
            skLineSegment(sketch, "E218.1.6", {"start": v(-12.33, -24.15) * mm, "end": v(-12.33, -30.66) * mm});
            skLineSegment(sketch, "E218.1.7", {"start": v(-12.33, -30.66) * mm, "end": v(-10, -33) * mm});
            skFitSpline(sketch, "E218.1.8", {"points": [v(-10, -33) * mm, v(-9.5, -33.24) * mm, v(-8.15, -33.73) * mm, v(-7.54, -33.85) * mm]});
            skLineSegment(sketch, "E218.1.9", {"start": v(-7.54, -33.85) * mm, "end": v(-4.46, -34.1) * mm});
            skLineSegment(sketch, "E218.1.10", {"start": v(-4.46, -34.1) * mm, "end": v(-4.96, -31.89) * mm});
            skLineSegment(sketch, "E218.1.11", {"start": v(-4.96, -31.89) * mm, "end": v(-6.92, -29.68) * mm});
            skLineSegment(sketch, "E218.1.12", {"start": v(-6.92, -29.68) * mm, "end": v(-5.57, -29.3) * mm});
            skLineSegment(sketch, "E218.1.13", {"start": v(-5.57, -29.3) * mm, "end": v(-2, -29.43) * mm});
            skLineSegment(sketch, "E218.1.14", {"start": v(-2, -29.43) * mm, "end": v(0.08, -28.2) * mm});
            skLineSegment(sketch, "E218.1.15", {"start": v(0.08, -28.2) * mm, "end": v(-0.16, -26.11) * mm});
            skLineSegment(sketch, "E218.1.16", {"start": v(-0.16, -26.11) * mm, "end": v(-3.36, -25.37) * mm});
            skLineSegment(sketch, "E218.1.17", {"start": v(-3.36, -25.37) * mm, "end": v(-3.6, -21.32) * mm});
            skLineSegment(sketch, "E218.1.18", {"start": v(-3.6, -21.32) * mm, "end": v(-2.74, -18.98) * mm});
            skLineSegment(sketch, "E218.1.19", {"start": v(-2.74, -18.98) * mm, "end": v(-2, -12.96) * mm});
            skLineSegment(sketch, "E218.1.20", {"start": v(-2, -12.96) * mm, "end": v(2.42, -12.72) * mm});
            skLineSegment(sketch, "E218.1.21", {"start": v(2.42, -12.72) * mm, "end": v(2.17, -6.2) * mm});
            skLineSegment(sketch, "E218.1.22", {"start": v(2.17, -6.2) * mm, "end": v(-0.04, -6.45) * mm});
            skLineSegment(sketch, "E218.1.23", {"start": v(-0.04, -6.45) * mm, "end": v(-1.27, -5.22) * mm});
            skLineSegment(sketch, "E218.1.24", {"start": v(-1.27, -5.22) * mm, "end": v(-1.64, -2.89) * mm});
            skLineSegment(sketch, "E218.1.25", {"start": v(-1.64, -2.89) * mm, "end": v(2.3, -3.13) * mm});
            skLineSegment(sketch, "E218.1.26", {"start": v(2.3, -3.13) * mm, "end": v(7.82, -2.89) * mm});
            skLineSegment(sketch, "E218.1.27", {"start": v(7.82, -2.89) * mm, "end": v(8.93, -1.9) * mm});
            skLineSegment(sketch, "E218.1.28", {"start": v(8.93, -1.9) * mm, "end": v(7.58, -0.67) * mm});
            skLineSegment(sketch, "E218.1.29", {"start": v(7.58, -0.67) * mm, "end": v(5.24, -0.06) * mm});
            skLineSegment(sketch, "E218.1.30", {"start": v(5.24, -0.06) * mm, "end": v(6.47, 0.92) * mm});
            skLineSegment(sketch, "E218.1.31", {"start": v(6.47, 0.92) * mm, "end": v(5.74, 2.28) * mm});
            skLineSegment(sketch, "E218.1.32", {"start": v(5.74, 2.28) * mm, "end": v(5.37, 1.54) * mm});
            skLineSegment(sketch, "E218.1.33", {"start": v(5.37, 1.54) * mm, "end": v(3.03, -0.06) * mm});
            skLineSegment(sketch, "E218.1.34", {"start": v(3.03, -0.06) * mm, "end": v(-1.52, 0.3) * mm});
            skLineSegment(sketch, "E218.1.35", {"start": v(-1.52, 0.3) * mm, "end": v(-1.88, 3.87) * mm});
            skLineSegment(sketch, "E218.1.36", {"start": v(-1.88, 3.87) * mm, "end": v(-1.76, 6.58) * mm});
            skLineSegment(sketch, "E218.1.37", {"start": v(-1.76, 6.58) * mm, "end": v(-2.5, 8.54) * mm});
            skLineSegment(sketch, "E218.1.38", {"start": v(-2.5, 8.54) * mm, "end": v(-3.36, 9.4) * mm});
            skLineSegment(sketch, "E218.1.39", {"start": v(-3.36, 9.4) * mm, "end": v(-4.34, 10.88) * mm});
            skLineSegment(sketch, "E218.1.40", {"start": v(-4.34, 10.88) * mm, "end": v(-3.36, 11.37) * mm});
            skLineSegment(sketch, "E218.1.41", {"start": v(-3.36, 11.37) * mm, "end": v(-1.88, 11.12) * mm});
            skLineSegment(sketch, "E218.1.42", {"start": v(-1.88, 11.12) * mm, "end": v(-1.88, 12.6) * mm});
            skLineSegment(sketch, "E218.1.43", {"start": v(-1.88, 12.6) * mm, "end": v(-1.02, 13.95) * mm});
            skLineSegment(sketch, "E218.1.44", {"start": v(-1.02, 13.95) * mm, "end": v(-1.4, 16.16) * mm});
            skLineSegment(sketch, "E218.1.45", {"start": v(-1.4, 16.16) * mm, "end": v(-1.27, 18.62) * mm});
            skLineSegment(sketch, "E218.1.46", {"start": v(-1.27, 18.62) * mm, "end": v(-3.6, 19.11) * mm});
            skLineSegment(sketch, "E218.1.47", {"start": v(-3.6, 19.11) * mm, "end": v(-6.8, 19.23) * mm});
            skLineSegment(sketch, "E218.1.48", {"start": v(-6.8, 19.23) * mm, "end": v(-8.64, 16.9) * mm});
            skLineSegment(sketch, "E218.1.49", {"start": v(-8.64, 16.9) * mm, "end": v(-8.77, 14.69) * mm});
            skLineSegment(sketch, "E218.1.50", {"start": v(-8.77, 14.69) * mm, "end": v(-7.41, 12.72) * mm});
            skLineSegment(sketch, "E218.1.51", {"start": v(-7.41, 12.72) * mm, "end": v(-8.4, 11.25) * mm});
            skLineSegment(sketch, "E218.1.52", {"start": v(-8.4, 11.25) * mm, "end": v(-9.26, 9.9) * mm});
            skLineSegment(sketch, "E218.1.53", {"start": v(-9.26, 9.9) * mm, "end": v(-10.73, 8.17) * mm});
            skLineSegment(sketch, "E218.1.54", {"start": v(-10.73, 8.17) * mm, "end": v(-11.22, 4.12) * mm});
            skLineSegment(sketch, "E218.1.55", {"start": v(-11.22, 4.12) * mm, "end": v(-10.6, -0.06) * mm});
            skSolve(sketch);
        }
        {
            var Q0;
            Q0=qCreatedBy(makeId("Top.planeOp"),FACE);
            var sketch = newSketch(context, id + "F2", { "sketchPlane" : qUnion([Q0])});
            skLineSegment(sketch, "E219.0", {"start": v(-63.17, -3.96) * mm, "end": v(-55.54, 15.54) * mm});
            skPoint(sketch, "E219.1", {"position": v(-49.32, 11.59) * mm});
            skLineSegment(sketch, "E219.2", {"start": v(-55.54, 15.54) * mm, "end": v(-49.32, 11.59) * mm});
            skLineSegment(sketch, "E219.3", {"start": v(-49.32, 11.59) * mm, "end": v(-44.8, 18.37) * mm});
            skLineSegment(sketch, "E219.4", {"start": v(-44.8, 18.37) * mm, "end": v(-51.86, 23.74) * mm});
            skLineSegment(sketch, "E219.5", {"start": v(-51.86, 23.74) * mm, "end": v(-50.17, 31.66) * mm});
            skLineSegment(sketch, "E219.6", {"start": v(-50.17, 31.66) * mm, "end": v(-40.84, 37.03) * mm});
            skLineSegment(sketch, "E219.7", {"start": v(-40.84, 37.03) * mm, "end": v(-34.9, 32.5) * mm});
            skLineSegment(sketch, "E219.8", {"start": v(-34.9, 32.5) * mm, "end": v(-28.4, 36.18) * mm});
            skLineSegment(sketch, "E219.9", {"start": v(-28.4, 36.18) * mm, "end": v(-31.23, 42.68) * mm});
            skLineSegment(sketch, "E219.10", {"start": v(-31.23, 42.68) * mm, "end": v(-13.14, 49.74) * mm});
            skLineSegment(sketch, "E219.11", {"start": v(-13.14, 49.74) * mm, "end": v(-10.03, 43.8) * mm});
            skLineSegment(sketch, "E219.12", {"start": v(-10.03, 43.8) * mm, "end": v(-4.66, 46.63) * mm});
            skLineSegment(sketch, "E219.13", {"start": v(-4.66, 46.63) * mm, "end": v(-1.84, 36.74) * mm});
            skLineSegment(sketch, "E219.14", {"start": v(-1.84, 36.74) * mm, "end": v(0.42, 36.74) * mm});
            skLineSegment(sketch, "E219.15", {"start": v(0.42, 36.74) * mm, "end": v(0.99, 62.74) * mm});
            skLineSegment(sketch, "E219.16", {"start": v(0.99, 62.74) * mm, "end": v(10.32, 66.7) * mm});
            skLineSegment(sketch, "E219.17", {"start": v(10.32, 66.7) * mm, "end": v(20.2, 60.2) * mm});
            skLineSegment(sketch, "E219.18", {"start": v(-55.82, -5.94) * mm, "end": v(-63.17, -3.96) * mm});
            skLineSegment(sketch, "E219.19", {"start": v(-56.67, -12.44) * mm, "end": v(-55.82, -5.94) * mm});
            skLineSegment(sketch, "E219.20", {"start": v(-46.5, -16.11) * mm, "end": v(-56.67, -12.44) * mm});
            skLineSegment(sketch, "E219.21", {"start": v(-45.93, -20.63) * mm, "end": v(-46.5, -16.11) * mm});
            skLineSegment(sketch, "E219.22", {"start": v(-54.4, -22.61) * mm, "end": v(-45.93, -20.63) * mm});
            skLineSegment(sketch, "E219.23", {"start": v(-55.54, -33.63) * mm, "end": v(-54.4, -22.61) * mm});
            skLineSegment(sketch, "E219.24", {"start": v(-50.45, -37.03) * mm, "end": v(-55.54, -33.63) * mm});
            skLineSegment(sketch, "E219.25", {"start": v(-41.12, -35.05) * mm, "end": v(-50.45, -37.03) * mm});
            skLineSegment(sketch, "E219.26", {"start": v(-38.58, -38.72) * mm, "end": v(-41.12, -35.05) * mm});
            skLineSegment(sketch, "E219.27", {"start": v(-44.23, -42.68) * mm, "end": v(-38.58, -38.72) * mm});
            skLineSegment(sketch, "E219.28", {"start": v(-38.86, -51.72) * mm, "end": v(-44.23, -42.68) * mm});
            skLineSegment(sketch, "E219.29", {"start": v(-28.69, -53.14) * mm, "end": v(-38.86, -51.72) * mm});
            skLineSegment(sketch, "E219.30", {"start": v(-26.14, -48.05) * mm, "end": v(-28.69, -53.14) * mm});
            skPoint(sketch, "E219.31", {"position": v(-24.73, -50.3) * mm});
            skPoint(sketch, "E219.32", {"position": v(-26.14, -48.05) * mm});
            skLineSegment(sketch, "E219.33", {"start": v(-24.73, -50.3) * mm, "end": v(-26.14, -48.05) * mm});
            skLineSegment(sketch, "E219.34", {"start": v(-27.27, -55.4) * mm, "end": v(-24.73, -50.3) * mm});
            skLineSegment(sketch, "E219.35", {"start": v(-18.51, -58.5) * mm, "end": v(-27.27, -55.4) * mm});
            skLineSegment(sketch, "E219.36", {"start": v(20.2, 60.2) * mm, "end": v(14, 37.87) * mm});
            skLineSegment(sketch, "E219.37", {"start": v(14, 37.87) * mm, "end": v(20.2, 35.61) * mm});
            skPoint(sketch, "E219.38", {"position": v(19.64, 33.92) * mm});
            skLineSegment(sketch, "E219.39", {"start": v(20.2, 35.61) * mm, "end": v(19.64, 33.92) * mm});
            skLineSegment(sketch, "E219.40", {"start": v(19.64, 33.92) * mm, "end": v(25.01, 31.37) * mm});
            skLineSegment(sketch, "E219.41", {"start": v(25.01, 31.37) * mm, "end": v(38.3, 50.03) * mm});
            skLineSegment(sketch, "E219.42", {"start": v(38.3, 50.03) * mm, "end": v(45.36, 48.05) * mm});
            skLineSegment(sketch, "E219.43", {"start": v(45.36, 48.05) * mm, "end": v(48.75, 48.9) * mm});
            skLineSegment(sketch, "E219.44", {"start": v(48.75, 48.9) * mm, "end": v(50.17, 39.29) * mm});
            skLineSegment(sketch, "E219.45", {"start": v(50.17, 39.29) * mm, "end": v(35.75, 24.87) * mm});
            skLineSegment(sketch, "E219.46", {"start": v(35.75, 24.87) * mm, "end": v(42.82, 14.98) * mm});
            skLineSegment(sketch, "E219.47", {"start": v(42.82, 14.98) * mm, "end": v(53.84, 21.48) * mm});
            skLineSegment(sketch, "E219.48", {"start": v(53.84, 21.48) * mm, "end": v(63.17, 15.54) * mm});
            skLineSegment(sketch, "E219.49", {"start": v(63.17, 15.54) * mm, "end": v(61.47, 2.54) * mm});
            skLineSegment(sketch, "E219.50", {"start": v(61.47, 2.54) * mm, "end": v(49.32, 0) * mm});
            skLineSegment(sketch, "E219.51", {"start": v(49.32, 0) * mm, "end": v(49.89, -6.22) * mm});
            skLineSegment(sketch, "E219.52", {"start": v(49.89, -6.22) * mm, "end": v(58.36, -17.52) * mm});
            skLineSegment(sketch, "E219.53", {"start": v(58.36, -17.52) * mm, "end": v(60.9, -19.22) * mm});
            skLineSegment(sketch, "E219.54", {"start": v(60.9, -19.22) * mm, "end": v(52.15, -41.55) * mm});
            skLineSegment(sketch, "E219.55", {"start": v(52.15, -41.55) * mm, "end": v(48.47, -39.29) * mm});
            skLineSegment(sketch, "E219.56", {"start": v(48.47, -39.29) * mm, "end": v(46.5, -45.22) * mm});
            skLineSegment(sketch, "E219.57", {"start": v(46.5, -45.22) * mm, "end": v(36.88, -50.03) * mm});
            skLineSegment(sketch, "E219.58", {"start": v(36.88, -50.03) * mm, "end": v(33.77, -47.48) * mm});
            skLineSegment(sketch, "E219.59", {"start": v(33.77, -47.48) * mm, "end": v(24.73, -53.42) * mm});
            skLineSegment(sketch, "E219.60", {"start": v(24.73, -53.42) * mm, "end": v(25.58, -55.68) * mm});
            skLineSegment(sketch, "E219.61", {"start": v(25.58, -55.68) * mm, "end": v(21.34, -62.18) * mm});
            skLineSegment(sketch, "E219.62", {"start": v(21.34, -62.18) * mm, "end": v(12.01, -61.33) * mm});
            skLineSegment(sketch, "E219.63", {"start": v(12.01, -61.33) * mm, "end": v(4.66, -63.31) * mm});
            skLineSegment(sketch, "E219.64", {"start": v(4.66, -63.31) * mm, "end": v(2.69, -58.79) * mm});
            skLineSegment(sketch, "E219.65", {"start": v(2.69, -58.79) * mm, "end": v(-1.84, -59.07) * mm});
            skLineSegment(sketch, "E219.66", {"start": v(-1.84, -59.07) * mm, "end": v(-1.84, -64.16) * mm});
            skLineSegment(sketch, "E219.67", {"start": v(-1.84, -64.16) * mm, "end": v(-9.19, -66.7) * mm});
            skLineSegment(sketch, "E219.68", {"start": v(-9.19, -66.7) * mm, "end": v(-18.8, -60.48) * mm});
            skLineSegment(sketch, "E219.69", {"start": v(-18.8, -60.48) * mm, "end": v(-18.51, -58.5) * mm});
            skPoint(sketch, "E219.70", {"position": v(-47.06, 14.98) * mm});
            skPoint(sketch, "E219.71", {"position": v(-48.33, 21.06) * mm});
            skPoint(sketch, "E219.72", {"position": v(-25.44, -49.18) * mm});
            skPoint(sketch, "E219.73", {"position": v(-22.9, -56.95) * mm});
            skSolve(sketch);
        }
        {
            var Q0;
            Q0=qCreatedBy(makeId("Top.planeOp"),FACE);
            var sketch = newSketch(context, id + "F3", { "sketchPlane" : qUnion([Q0])});
            skFitSpline(sketch, "E220", {"points": [v(0.46, -36.46) * mm, v(43.84, -30.83) * mm, v(93.02, -14.87) * mm, v(126.2, 4.34) * mm]});
            skFitSpline(sketch, "E221", {"points": [v(126.2, 4.34) * mm, v(132.1, 7.75) * mm, v(133.86, 8.4) * mm, v(137.24, 8.4) * mm]});
            skFitSpline(sketch, "E222", {"points": [v(137.24, 8.4) * mm, v(139.44, 8.4) * mm, v(142.44, 8.9) * mm, v(143.9, 9.5) * mm]});
            skFitSpline(sketch, "E223", {"points": [v(143.9, 9.5) * mm, v(145.8, 10.3) * mm, v(146.95, 10.38) * mm, v(148.02, 9.78) * mm]});
            skFitSpline(sketch, "E224", {"points": [v(148.02, 9.78) * mm, v(149, 9.23) * mm, v(157.9, 9.11) * mm, v(174.66, 9.44) * mm]});
            skFitSpline(sketch, "E225", {"points": [v(174.66, 9.44) * mm, v(198.63, 9.9) * mm, v(199.9, 10) * mm, v(201.57, 11.57) * mm]});
            skFitSpline(sketch, "E226", {"points": [v(204.79, 11.61) * mm, v(205.9, 10.4) * mm, v(207.25, 10) * mm, v(210.37, 10) * mm]});
            skFitSpline(sketch, "E227", {"points": [v(210.37, 10) * mm, v(217.53, 10) * mm, v(217.45, 9.78) * mm, v(216.4, 26.81) * mm]});
            skFitSpline(sketch, "E228", {"points": [v(216.4, 26.81) * mm, v(215.9, 34.93) * mm, v(215.1, 42.03) * mm, v(214.65, 42.59) * mm]});
            skFitSpline(sketch, "E229", {"points": [v(214.65, 42.59) * mm, v(213.73, 43.69) * mm, v(203.86, 44) * mm, v(202.31, 42.99) * mm]});
            skFitSpline(sketch, "E230", {"points": [v(202.31, 42.99) * mm, v(201.82, 42.66) * mm, v(200.74, 41.14) * mm, v(199.91, 39.6) * mm]});
            skLineSegment(sketch, "E231", {"start": v(201.57, 11.57) * mm, "end": v(203.33, 13.22) * mm});
            skLineSegment(sketch, "E232", {"start": v(203.33, 13.22) * mm, "end": v(204.79, 11.61) * mm});
            skFitSpline(sketch, "E233", {"points": [v(198.15, 39.44) * mm, v(197.96, 41.33) * mm, v(197.33, 42.34) * mm, v(195.92, 42.98) * mm]});
            skFitSpline(sketch, "E234", {"points": [v(195.92, 42.98) * mm, v(194.54, 43.6) * mm, v(194.1, 44.27) * mm, v(194.5, 45.14) * mm]});
            skFitSpline(sketch, "E235", {"points": [v(194.5, 45.14) * mm, v(194.8, 45.83) * mm, v(195.08, 47.3) * mm, v(195.12, 48.4) * mm]});
            skFitSpline(sketch, "E236", {"points": [v(195.12, 48.4) * mm, v(195.2, 50.2) * mm, v(194.86, 50.42) * mm, v(191.66, 50.65) * mm]});
            skFitSpline(sketch, "E237", {"points": [v(191.66, 50.65) * mm, v(186.16, 51.05) * mm, v(184.73, 50.38) * mm, v(183.29, 46.79) * mm]});
            skFitSpline(sketch, "E238", {"points": [v(183.29, 46.79) * mm, v(182.28, 44.26) * mm, v(181.47, 43.45) * mm, v(179.58, 43.08) * mm]});
            skFitSpline(sketch, "E239", {"points": [v(179.58, 43.08) * mm, v(178.25, 42.81) * mm, v(176.97, 42.28) * mm, v(176.74, 41.9) * mm]});
            skFitSpline(sketch, "E240", {"points": [v(176.74, 41.9) * mm, v(176.03, 40.75) * mm, v(173.5, 41.1) * mm, v(171.69, 42.6) * mm]});
            skFitSpline(sketch, "E241", {"points": [v(171.69, 42.6) * mm, v(170.05, 43.96) * mm, v(170.04, 44.13) * mm, v(171.26, 48) * mm]});
            skFitSpline(sketch, "E242", {"points": [v(171.26, 48) * mm, v(173.87, 56.3) * mm, v(171.26, 65.23) * mm, v(164.6, 70.79) * mm]});
            skFitSpline(sketch, "E243", {"points": [v(164.6, 70.79) * mm, v(158.01, 76.28) * mm, v(145.57, 80.7) * mm, v(130.4, 82.92) * mm]});
            skFitSpline(sketch, "E244", {"points": [v(130.4, 82.92) * mm, v(122.04, 84.15) * mm, v(93.5, 84.12) * mm, v(82.8, 82.87) * mm]});
            skFitSpline(sketch, "E245", {"points": [v(82.8, 82.87) * mm, v(36.22, 77.45) * mm, v(-11.28, 63.02) * mm, v(-46.9, 43.46) * mm]});
            skFitSpline(sketch, "E246", {"points": [v(-46.9, 43.46) * mm, v(-54.82, 39.12) * mm, v(-55.75, 38.8) * mm, v(-60.64, 38.8) * mm]});
            skFitSpline(sketch, "E247", {"points": [v(-60.64, 38.8) * mm, v(-66.62, 38.8) * mm, v(-67.93, 37.97) * mm, v(-68.74, 33.64) * mm]});
            skFitSpline(sketch, "E248", {"points": [v(-68.74, 33.64) * mm, v(-69.37, 30.27) * mm, v(-70.8, 29.85) * mm, v(-70.8, 33.02) * mm]});
            skFitSpline(sketch, "E249", {"points": [v(-70.8, 33.02) * mm, v(-70.8, 34.24) * mm, v(-71.36, 36.04) * mm, v(-72.05, 37.02) * mm]});
            skFitSpline(sketch, "E250", {"points": [v(-72.05, 37.02) * mm, v(-73.09, 38.5) * mm, v(-74.04, 38.8) * mm, v(-77.85, 38.79) * mm]});
            skFitSpline(sketch, "E251", {"points": [v(-77.85, 38.79) * mm, v(-84.98, 38.77) * mm, v(-85.73, 38.07) * mm, v(-90.8, 26.8) * mm]});
            skFitSpline(sketch, "E252", {"points": [v(-90.8, 26.8) * mm, v(-95.09, 17.24) * mm, v(-95.4, 16.79) * mm, v(-97.84, 16.55) * mm]});
            skFitSpline(sketch, "E253", {"points": [v(-97.84, 16.55) * mm, v(-100.92, 16.25) * mm, v(-100.9, 15.93) * mm, v(-98.7, 26.95) * mm]});
            skFitSpline(sketch, "E254", {"points": [v(-98.7, 26.95) * mm, v(-97.76, 31.66) * mm, v(-97.2, 36.07) * mm, v(-97.47, 36.75) * mm]});
            skFitSpline(sketch, "E255", {"points": [v(-97.47, 36.75) * mm, v(-97.84, 37.71) * mm, v(-99.2, 38) * mm, v(-103.41, 38) * mm]});
            skFitSpline(sketch, "E256", {"points": [v(-103.41, 38) * mm, v(-106.52, 38) * mm, v(-109.28, 37.6) * mm, v(-109.81, 37.07) * mm]});
            skFitSpline(sketch, "E257", {"points": [v(-109.81, 37.07) * mm, v(-110.53, 36.35) * mm, v(-111.49, 36.35) * mm, v(-113.87, 37.07) * mm]});
            skFitSpline(sketch, "E258", {"points": [v(-113.87, 37.07) * mm, v(-118.62, 38.49) * mm, v(-131.16, 38.3) * mm, v(-132.42, 36.78) * mm]});
            skFitSpline(sketch, "E259", {"points": [v(-132.42, 36.78) * mm, v(-133.48, 35.5) * mm, v(-138.8, 10.47) * mm, v(-138.8, 6.74) * mm]});
            skFitSpline(sketch, "E260", {"points": [v(-138.8, 6.74) * mm, v(-138.8, 4.18) * mm, v(-137.64, 3.6) * mm, v(-132.49, 3.6) * mm]});
            skFitSpline(sketch, "E261", {"points": [v(-132.49, 3.6) * mm, v(-127.5, 3.6) * mm, v(-126.1, 4.78) * mm, v(-124.95, 9.93) * mm]});
            skLineSegment(sketch, "E262", {"start": v(199.91, 39.6) * mm, "end": v(198.4, 36.8) * mm});
            skLineSegment(sketch, "E263", {"start": v(198.4, 36.8) * mm, "end": v(198.15, 39.44) * mm});
            skLineSegment(sketch, "E264", {"start": v(198.15, 39.44) * mm, "end": v(199.91, 39.6) * mm});
            skFitSpline(sketch, "E265", {"points": [v(-119.68, 15.32) * mm, v(-117.3, 15.93) * mm, v(-115.2, 16.27) * mm, v(-115.01, 16.08) * mm]});
            skFitSpline(sketch, "E266", {"points": [v(-115.01, 16.08) * mm, v(-114.82, 15.88) * mm, v(-115.08, 13.7) * mm, v(-115.6, 11.22) * mm]});
            skFitSpline(sketch, "E267", {"points": [v(-115.6, 11.22) * mm, v(-116.97, 4.6) * mm, v(-116.65, 4.4) * mm, v(-104.84, 4.4) * mm]});
            skFitSpline(sketch, "E268", {"points": [v(-104.84, 4.4) * mm, v(-99.46, 4.4) * mm, v(-94.86, 4.19) * mm, v(-94.6, 3.93) * mm]});
            skFitSpline(sketch, "E269", {"points": [v(-94.6, 3.93) * mm, v(-94.34, 3.68) * mm, v(-94.85, 1.43) * mm, v(-95.73, -1.07) * mm]});
            skFitSpline(sketch, "E270", {"points": [v(-95.73, -1.07) * mm, v(-99.1, -10.65) * mm, v(-96.3, -19.8) * mm, v(-88.13, -25.97) * mm]});
            skFitSpline(sketch, "E271", {"points": [v(-88.13, -25.97) * mm, v(-79.4, -32.56) * mm, v(-66.96, -36.24) * mm, v(-46.4, -38.33) * mm]});
            skFitSpline(sketch, "E272", {"points": [v(-46.4, -38.33) * mm, v(-38.88, -39.09) * mm, v(-11.3, -38) * mm, v(0.46, -36.46) * mm]});
            skLineSegment(sketch, "E273", {"start": v(-124.95, 9.93) * mm, "end": v(-124, 14.22) * mm});
            skLineSegment(sketch, "E274", {"start": v(-124, 14.22) * mm, "end": v(-119.68, 15.32) * mm});
            skFitSpline(sketch, "E275", {"points": [v(-136.09, 7.13) * mm, v(-136.64, 8.57) * mm, v(-131.72, 33.25) * mm, v(-130.62, 34.6) * mm]});
            skFitSpline(sketch, "E276", {"points": [v(-130.62, 34.6) * mm, v(-129.53, 35.93) * mm, v(-117.46, 35.91) * mm, v(-114.81, 34.57) * mm]});
            skFitSpline(sketch, "E277", {"points": [v(-114.81, 34.57) * mm, v(-108.27, 31.26) * mm, v(-112.66, 18.94) * mm, v(-120.86, 17.62) * mm]});
            skFitSpline(sketch, "E278", {"points": [v(-120.86, 17.62) * mm, v(-125.57, 16.86) * mm, v(-126.33, 16.18) * mm, v(-127.2, 11.91) * mm]});
            skFitSpline(sketch, "E279", {"points": [v(-127.2, 11.91) * mm, v(-127.64, 9.76) * mm, v(-128.3, 7.55) * mm, v(-128.65, 7) * mm]});
            skFitSpline(sketch, "E280", {"points": [v(-128.65, 7) * mm, v(-129.56, 5.6) * mm, v(-135.54, 5.7) * mm, v(-136.09, 7.13) * mm]});
            skFitSpline(sketch, "E281", {"points": [v(-121.2, 26.85) * mm, v(-121.2, 29.05) * mm, v(-122.6, 29.46) * mm, v(-123.62, 27.56) * mm]});
            skFitSpline(sketch, "E282", {"points": [v(-123.62, 27.56) * mm, v(-124.87, 25.23) * mm, v(-124.02, 23.06) * mm, v(-122.4, 24.4) * mm]});
            skFitSpline(sketch, "E283", {"points": [v(-122.4, 24.4) * mm, v(-121.74, 24.95) * mm, v(-121.2, 26.05) * mm, v(-121.2, 26.85) * mm]});
            skFitSpline(sketch, "E284", {"points": [v(-113.2, 8.68) * mm, v(-113.2, 10.92) * mm, v(-108.63, 33.78) * mm, v(-107.97, 34.85) * mm]});
            skFitSpline(sketch, "E285", {"points": [v(-107.97, 34.85) * mm, v(-107.42, 35.74) * mm, v(-100.66, 35.86) * mm, v(-100.12, 35) * mm]});
            skFitSpline(sketch, "E286", {"points": [v(-100.12, 35) * mm, v(-99.91, 34.66) * mm, v(-100.64, 29.95) * mm, v(-101.74, 24.52) * mm]});
            skFitSpline(sketch, "E287", {"points": [v(-101.74, 24.52) * mm, v(-102.83, 19.1) * mm, v(-103.6, 14.55) * mm, v(-103.46, 14.41) * mm]});
            skFitSpline(sketch, "E288", {"points": [v(-103.46, 14.41) * mm, v(-103.32, 14.27) * mm, v(-101.1, 14.03) * mm, v(-98.52, 13.88) * mm]});
            skFitSpline(sketch, "E289", {"points": [v(-89.16, 24.33) * mm, v(-86.58, 30.23) * mm, v(-84, 35.36) * mm, v(-83.44, 35.72) * mm]});
            skFitSpline(sketch, "E290", {"points": [v(-83.44, 35.72) * mm, v(-81.82, 36.74) * mm, v(-75.09, 36.51) * mm, v(-74.2, 35.4) * mm]});
            skFitSpline(sketch, "E291", {"points": [v(-74.2, 35.4) * mm, v(-73.75, 34.85) * mm, v(-73.26, 28.46) * mm, v(-73.1, 21.2) * mm]});
            skLineSegment(sketch, "E292", {"start": v(-98.52, 13.88) * mm, "end": v(-93.84, 13.6) * mm});
            skLineSegment(sketch, "E293", {"start": v(-93.84, 13.6) * mm, "end": v(-89.16, 24.33) * mm});
            skFitSpline(sketch, "E294", {"points": [v(-76.6, 7.76) * mm, v(-80.05, 7.54) * mm, v(-80.48, 7.7) * mm, v(-81.18, 9.56) * mm]});
            skFitSpline(sketch, "E295", {"points": [v(-81.18, 9.56) * mm, v(-82.2, 12.22) * mm, v(-85.54, 12.36) * mm, v(-86.9, 9.8) * mm]});
            skFitSpline(sketch, "E296", {"points": [v(-86.9, 9.8) * mm, v(-87.41, 8.81) * mm, v(-88.24, 7.74) * mm, v(-88.72, 7.41) * mm]});
            skFitSpline(sketch, "E297", {"points": [v(-88.72, 7.41) * mm, v(-89.2, 7.09) * mm, v(-94.9, 6.82) * mm, v(-101.4, 6.81) * mm]});
            skLineSegment(sketch, "E298", {"start": v(-73.1, 21.2) * mm, "end": v(-72.8, 8) * mm});
            skLineSegment(sketch, "E299", {"start": v(-72.8, 8) * mm, "end": v(-76.6, 7.76) * mm});
            skFitSpline(sketch, "E300", {"points": [v(-80.4, 21.7) * mm, v(-80.4, 22.74) * mm, v(-80.77, 23.6) * mm, v(-81.22, 23.6) * mm]});
            skFitSpline(sketch, "E301", {"points": [v(-81.22, 23.6) * mm, v(-82.26, 23.6) * mm, v(-83.77, 19.72) * mm, v(-83.13, 18.7) * mm]});
            skFitSpline(sketch, "E302", {"points": [v(-83.13, 18.7) * mm, v(-82.36, 17.44) * mm, v(-80.4, 19.6) * mm, v(-80.4, 21.7) * mm]});
            skLineSegment(sketch, "E303", {"start": v(-101.4, 6.81) * mm, "end": v(-113.2, 6.8) * mm});
            skLineSegment(sketch, "E304", {"start": v(-113.2, 6.8) * mm, "end": v(-113.2, 8.68) * mm});
            skFitSpline(sketch, "E305", {"points": [v(-71.17, 8.36) * mm, v(-71.46, 8.82) * mm, v(-71.47, 9.56) * mm, v(-71.2, 10) * mm]});
            skFitSpline(sketch, "E306", {"points": [v(-71.2, 10) * mm, v(-70.93, 10.43) * mm, v(-69.67, 16.2) * mm, v(-68.4, 22.8) * mm]});
            skFitSpline(sketch, "E307", {"points": [v(-68.4, 22.8) * mm, v(-67.13, 29.4) * mm, v(-65.87, 35.17) * mm, v(-65.6, 35.6) * mm]});
            skFitSpline(sketch, "E308", {"points": [v(-65.6, 35.6) * mm, v(-65.33, 36.04) * mm, v(-63.37, 36.4) * mm, v(-61.24, 36.4) * mm]});
            skFitSpline(sketch, "E309", {"points": [v(-61.24, 36.4) * mm, v(-56.8, 36.4) * mm, v(-56.4, 35.88) * mm, v(-56.4, 29.93) * mm]});
            skFitSpline(sketch, "E310", {"points": [v(-56.4, 29.93) * mm, v(-56.4, 24.49) * mm, v(-55.15, 25.01) * mm, v(-53.87, 31) * mm]});
            skFitSpline(sketch, "E311", {"points": [v(-49.7, 36.25) * mm, v(-47.98, 36.4) * mm, v(-46.28, 36.2) * mm, v(-45.9, 35.82) * mm]});
            skFitSpline(sketch, "E312", {"points": [v(-45.9, 35.82) * mm, v(-45.1, 35.03) * mm, v(-49.81, 10.16) * mm, v(-51.05, 8.56) * mm]});
            skFitSpline(sketch, "E313", {"points": [v(-51.05, 8.56) * mm, v(-51.56, 7.9) * mm, v(-53.22, 7.61) * mm, v(-55.53, 7.76) * mm]});
            skFitSpline(sketch, "E314", {"points": [v(-55.53, 7.76) * mm, v(-58.78, 7.97) * mm, v(-59.22, 8.23) * mm, v(-59.41, 10) * mm]});
            skFitSpline(sketch, "E315", {"points": [v(-59.41, 10) * mm, v(-60.05, 16.05) * mm, v(-60.57, 18.9) * mm, v(-60.97, 18.5) * mm]});
            skFitSpline(sketch, "E316", {"points": [v(-60.97, 18.5) * mm, v(-61.21, 18.26) * mm, v(-62, 15.8) * mm, v(-62.72, 13.03) * mm]});
            skLineSegment(sketch, "E317", {"start": v(-53.87, 31) * mm, "end": v(-52.8, 36) * mm});
            skLineSegment(sketch, "E318", {"start": v(-52.8, 36) * mm, "end": v(-49.7, 36.25) * mm});
            skFitSpline(sketch, "E319", {"points": [v(-67.34, 7.76) * mm, v(-69.16, 7.62) * mm, v(-70.89, 7.9) * mm, v(-71.17, 8.36) * mm]});
            skLineSegment(sketch, "E320", {"start": v(-62.72, 13.03) * mm, "end": v(-64.03, 8) * mm});
            skLineSegment(sketch, "E321", {"start": v(-64.03, 8) * mm, "end": v(-67.34, 7.76) * mm});
            skFitSpline(sketch, "E322", {"points": [v(-46.47, 8.35) * mm, v(-47.1, 9) * mm, v(-46.64, 12.9) * mm, v(-44.8, 22.43) * mm]});
            skFitSpline(sketch, "E323", {"points": [v(-44.8, 22.43) * mm, v(-43.41, 29.67) * mm, v(-42.02, 35.85) * mm, v(-41.7, 36.16) * mm]});
            skFitSpline(sketch, "E324", {"points": [v(-41.7, 36.16) * mm, v(-41.4, 36.47) * mm, v(-28.92, 36.84) * mm, v(-13.97, 36.99) * mm]});
            skFitSpline(sketch, "E325", {"points": [v(13.2, 34.99) * mm, v(13.2, 31.87) * mm, v(11.86, 30.8) * mm, v(7.94, 30.8) * mm]});
            skFitSpline(sketch, "E326", {"points": [v(7.94, 30.8) * mm, v(4.56, 30.8) * mm, v(2.2, 29.23) * mm, v(3.18, 27.64) * mm]});
            skFitSpline(sketch, "E327", {"points": [v(3.18, 27.64) * mm, v(3.46, 27.18) * mm, v(5.12, 26.8) * mm, v(6.87, 26.8) * mm]});
            skFitSpline(sketch, "E328", {"points": [v(6.87, 26.8) * mm, v(10.5, 26.8) * mm, v(11.52, 25.41) * mm, v(10.12, 22.35) * mm]});
            skFitSpline(sketch, "E329", {"points": [v(10.12, 22.35) * mm, v(9.41, 20.79) * mm, v(8.63, 20.4) * mm, v(6.22, 20.39) * mm]});
            skFitSpline(sketch, "E330", {"points": [v(6.22, 20.39) * mm, v(2.62, 20.37) * mm, v(1.45, 19.74) * mm, v(1.08, 17.6) * mm]});
            skFitSpline(sketch, "E331", {"points": [v(1.08, 17.6) * mm, v(0.84, 16.22) * mm, v(1.34, 15.95) * mm, v(4.8, 15.6) * mm]});
            skFitSpline(sketch, "E332", {"points": [v(4.8, 15.6) * mm, v(8.53, 15.23) * mm, v(8.82, 15.04) * mm, v(9.07, 12.84) * mm]});
            skFitSpline(sketch, "E333", {"points": [v(9.07, 12.84) * mm, v(9.48, 9.26) * mm, v(7.62, 8.4) * mm, v(-0.58, 8.4) * mm]});
            skFitSpline(sketch, "E334", {"points": [v(-0.58, 8.4) * mm, v(-6.15, 8.4) * mm, v(-7.75, 8.66) * mm, v(-8.11, 9.6) * mm]});
            skFitSpline(sketch, "E335", {"points": [v(-8.11, 9.6) * mm, v(-8.37, 10.28) * mm, v(-7.82, 14.9) * mm, v(-6.89, 19.88) * mm]});
            skFitSpline(sketch, "E336", {"points": [v(-6.89, 19.88) * mm, v(-5.96, 24.87) * mm, v(-5.2, 29.36) * mm, v(-5.2, 29.85) * mm]});
            skFitSpline(sketch, "E337", {"points": [v(-5.2, 29.85) * mm, v(-5.2, 31.07) * mm, v(-10.12, 30.15) * mm, v(-11.27, 28.72) * mm]});
            skFitSpline(sketch, "E338", {"points": [v(-11.27, 28.72) * mm, v(-11.76, 28.12) * mm, v(-12.8, 23.94) * mm, v(-13.58, 19.42) * mm]});
            skFitSpline(sketch, "E339", {"points": [v(-13.58, 19.42) * mm, v(-15.44, 8.65) * mm, v(-15.67, 8.25) * mm, v(-19.85, 8.56) * mm]});
            skFitSpline(sketch, "E340", {"points": [v(-19.85, 8.56) * mm, v(-23.78, 8.84) * mm, v(-23.7, 8.23) * mm, v(-21.55, 20.56) * mm]});
            skFitSpline(sketch, "E341", {"points": [v(-21.55, 20.56) * mm, v(-20.73, 25.27) * mm, v(-20.32, 29.4) * mm, v(-20.65, 29.71) * mm]});
            skFitSpline(sketch, "E342", {"points": [v(-20.65, 29.71) * mm, v(-21.67, 30.74) * mm, v(-34.23, 30.12) * mm, v(-34.93, 29.01) * mm]});
            skFitSpline(sketch, "E343", {"points": [v(-34.93, 29.01) * mm, v(-36.07, 27.22) * mm, v(-35.15, 26.4) * mm, v(-31.7, 26.15) * mm]});
            skFitSpline(sketch, "E344", {"points": [v(-31.7, 26.15) * mm, v(-27.91, 25.87) * mm, v(-27.15, 24.88) * mm, v(-28.35, 21.74) * mm]});
            skFitSpline(sketch, "E345", {"points": [v(-28.35, 21.74) * mm, v(-29.06, 19.86) * mm, v(-29.6, 19.6) * mm, v(-32.75, 19.6) * mm]});
            skFitSpline(sketch, "E346", {"points": [v(-32.75, 19.6) * mm, v(-35.59, 19.6) * mm, v(-36.53, 19.24) * mm, v(-37.25, 17.91) * mm]});
            skFitSpline(sketch, "E347", {"points": [v(-37.25, 17.91) * mm, v(-38.44, 15.68) * mm, v(-37.53, 14.95) * mm, v(-33.2, 14.65) * mm]});
            skFitSpline(sketch, "E348", {"points": [v(-33.2, 14.65) * mm, v(-30.03, 14.43) * mm, v(-29.58, 14.16) * mm, v(-29.4, 12.4) * mm]});
            skFitSpline(sketch, "E349", {"points": [v(-29.4, 12.4) * mm, v(-29.28, 11.3) * mm, v(-29.47, 9.96) * mm, v(-29.82, 9.43) * mm]});
            skFitSpline(sketch, "E350", {"points": [v(-29.82, 9.43) * mm, v(-30.71, 8.07) * mm, v(-45.3, 7.12) * mm, v(-46.47, 8.35) * mm]});
            skLineSegment(sketch, "E351", {"start": v(-13.97, 36.99) * mm, "end": v(13.2, 37.26) * mm});
            skLineSegment(sketch, "E352", {"start": v(13.2, 37.26) * mm, "end": v(13.2, 34.99) * mm});
            skFitSpline(sketch, "E353", {"points": [v(133.44, 10.89) * mm, v(130.3, 11.8) * mm, v(128.4, 14.34) * mm, v(128.42, 17.58) * mm]});
            skFitSpline(sketch, "E354", {"points": [v(128.42, 17.58) * mm, v(128.45, 21.53) * mm, v(131.4, 33.76) * mm, v(132.88, 36) * mm]});
            skFitSpline(sketch, "E355", {"points": [v(132.88, 36) * mm, v(135.38, 39.83) * mm, v(141.66, 41.78) * mm, v(146.9, 40.37) * mm]});
            skFitSpline(sketch, "E356", {"points": [v(146.9, 40.37) * mm, v(150.39, 39.43) * mm, v(151.6, 37.73) * mm, v(151.6, 33.75) * mm]});
            skFitSpline(sketch, "E357", {"points": [v(151.6, 33.75) * mm, v(151.6, 30.26) * mm, v(150.11, 29.03) * mm, v(146.26, 29.35) * mm]});
            skFitSpline(sketch, "E358", {"points": [v(146.26, 29.35) * mm, v(143.94, 29.54) * mm, v(143.15, 29.98) * mm, v(142.96, 31.2) * mm]});
            skFitSpline(sketch, "E359", {"points": [v(142.96, 31.2) * mm, v(142.03, 37.04) * mm, v(140.73, 35.43) * mm, v(138.81, 26.06) * mm]});
            skFitSpline(sketch, "E360", {"points": [v(138.81, 26.06) * mm, v(137.98, 22) * mm, v(137.49, 18.18) * mm, v(137.72, 17.59) * mm]});
            skFitSpline(sketch, "E361", {"points": [v(137.72, 17.59) * mm, v(138.35, 15.93) * mm, v(140.19, 17.05) * mm, v(140.8, 19.45) * mm]});
            skFitSpline(sketch, "E362", {"points": [v(140.8, 19.45) * mm, v(141.09, 20.63) * mm, v(141.7, 22.04) * mm, v(142.16, 22.6) * mm]});
            skFitSpline(sketch, "E363", {"points": [v(142.16, 22.6) * mm, v(143.18, 23.82) * mm, v(148.9, 23.93) * mm, v(149.64, 22.74) * mm]});
            skFitSpline(sketch, "E364", {"points": [v(149.64, 22.74) * mm, v(150.4, 21.49) * mm, v(147.86, 15.32) * mm, v(145.78, 13.4) * mm]});
            skFitSpline(sketch, "E365", {"points": [v(145.78, 13.4) * mm, v(144.16, 11.9) * mm, v(138.77, 9.9) * mm, v(136.8, 10.08) * mm]});
            skFitSpline(sketch, "E366", {"points": [v(136.8, 10.08) * mm, v(136.36, 10.11) * mm, v(134.85, 10.48) * mm, v(133.44, 10.89) * mm]});
            skFitSpline(sketch, "E367", {"points": [v(151, 11.33) * mm, v(150.45, 11.55) * mm, v(150.01, 12.51) * mm, v(150.03, 13.47) * mm]});
            skFitSpline(sketch, "E368", {"points": [v(150.03, 13.47) * mm, v(150.07, 16.48) * mm, v(154.62, 38.94) * mm, v(155.32, 39.64) * mm]});
            skFitSpline(sketch, "E369", {"points": [v(155.32, 39.64) * mm, v(156.18, 40.49) * mm, v(169.04, 40.9) * mm, v(171.28, 40.14) * mm]});
            skFitSpline(sketch, "E370", {"points": [v(171.28, 40.14) * mm, v(174.81, 38.94) * mm, v(175.34, 34.3) * mm, v(172.56, 28.8) * mm]});
            skFitSpline(sketch, "E371", {"points": [v(172.56, 28.8) * mm, v(171.82, 27.33) * mm, v(171.3, 23.83) * mm, v(171.2, 19.77) * mm]});
            skFitSpline(sketch, "E372", {"points": [v(171.2, 19.77) * mm, v(171.12, 16.12) * mm, v(170.69, 12.77) * mm, v(170.24, 12.32) * mm]});
            skFitSpline(sketch, "E373", {"points": [v(170.24, 12.32) * mm, v(169.79, 11.87) * mm, v(167.84, 11.61) * mm, v(165.9, 11.75) * mm]});
            skFitSpline(sketch, "E374", {"points": [v(162.63, 17) * mm, v(162.81, 20.91) * mm, v(162.61, 22) * mm, v(161.72, 22) * mm]});
            skFitSpline(sketch, "E375", {"points": [v(161.72, 22) * mm, v(160.34, 22) * mm, v(159.9, 20.98) * mm, v(159.17, 16.1) * mm]});
            skFitSpline(sketch, "E376", {"points": [v(159.17, 16.1) * mm, v(158.87, 14.05) * mm, v(158.39, 12.25) * mm, v(158.1, 12.1) * mm]});
            skFitSpline(sketch, "E377", {"points": [v(158.1, 12.1) * mm, v(157.04, 11.5) * mm, v(151.95, 10.95) * mm, v(151, 11.33) * mm]});
            skLineSegment(sketch, "E378", {"start": v(165.9, 11.75) * mm, "end": v(162.4, 12) * mm});
            skLineSegment(sketch, "E379", {"start": v(162.4, 12) * mm, "end": v(162.63, 17) * mm});
            skFitSpline(sketch, "E380", {"points": [v(164.83, 30.88) * mm, v(165.42, 32.76) * mm, v(164.2, 34.47) * mm, v(162.87, 33.64) * mm]});
            skFitSpline(sketch, "E381", {"points": [v(162.87, 33.64) * mm, v(162.4, 33.35) * mm, v(162, 32.23) * mm, v(162, 31.15) * mm]});
            skFitSpline(sketch, "E382", {"points": [v(162, 31.15) * mm, v(162, 28.73) * mm, v(164.08, 28.53) * mm, v(164.83, 30.88) * mm]});
            skFitSpline(sketch, "E383", {"points": [v(173.53, 12.68) * mm, v(173.05, 13.94) * mm, v(176.86, 36.69) * mm, v(178, 39.4) * mm]});
            skFitSpline(sketch, "E384", {"points": [v(178, 39.4) * mm, v(178.62, 40.85) * mm, v(179.4, 41.2) * mm, v(182.04, 41.2) * mm]});
            skFitSpline(sketch, "E385", {"points": [v(182.04, 41.2) * mm, v(184.92, 41.2) * mm, v(185.25, 41.38) * mm, v(184.8, 42.77) * mm]});
            skFitSpline(sketch, "E386", {"points": [v(184.8, 42.77) * mm, v(184.3, 44.38) * mm, v(185.55, 47.54) * mm, v(187.12, 48.59) * mm]});
            skFitSpline(sketch, "E387", {"points": [v(187.12, 48.59) * mm, v(188.32, 49.39) * mm, v(190.96, 49.33) * mm, v(192.3, 48.47) * mm]});
            skFitSpline(sketch, "E388", {"points": [v(192.3, 48.47) * mm, v(193.2, 47.9) * mm, v(193, 47.24) * mm, v(191.3, 45.01) * mm]});
            skFitSpline(sketch, "E389", {"points": [v(191.3, 45.01) * mm, v(190.15, 43.5) * mm, v(189.2, 42.01) * mm, v(189.2, 41.72) * mm]});
            skFitSpline(sketch, "E390", {"points": [v(189.2, 41.72) * mm, v(189.2, 41.44) * mm, v(190.64, 41.2) * mm, v(192.4, 41.2) * mm]});
            skFitSpline(sketch, "E391", {"points": [v(192.4, 41.2) * mm, v(195.37, 41.2) * mm, v(195.6, 41.04) * mm, v(195.6, 38.95) * mm]});
            skFitSpline(sketch, "E392", {"points": [v(195.6, 38.95) * mm, v(195.6, 35.4) * mm, v(194.07, 34.1) * mm, v(189.6, 33.83) * mm]});
            skFitSpline(sketch, "E393", {"points": [v(189.6, 33.83) * mm, v(186.21, 33.64) * mm, v(185.6, 33.36) * mm, v(185.6, 32) * mm]});
            skFitSpline(sketch, "E394", {"points": [v(185.6, 32) * mm, v(185.6, 30.69) * mm, v(186.22, 30.36) * mm, v(189.04, 30.15) * mm]});
            skFitSpline(sketch, "E395", {"points": [v(189.04, 30.15) * mm, v(192.89, 29.88) * mm, v(193.65, 28.89) * mm, v(192.45, 25.74) * mm]});
            skFitSpline(sketch, "E396", {"points": [v(192.45, 25.74) * mm, v(191.76, 23.92) * mm, v(191.17, 23.6) * mm, v(188.48, 23.6) * mm]});
            skFitSpline(sketch, "E397", {"points": [v(188.48, 23.6) * mm, v(181.89, 23.6) * mm, v(181.13, 18.88) * mm, v(187.69, 18.68) * mm]});
            skFitSpline(sketch, "E398", {"points": [v(187.69, 18.68) * mm, v(189.84, 18.61) * mm, v(192.02, 18.52) * mm, v(192.54, 18.48) * mm]});
            skFitSpline(sketch, "E399", {"points": [v(192.54, 18.48) * mm, v(193.06, 18.44) * mm, v(195.56, 23.39) * mm, v(198.1, 29.48) * mm]});
            skFitSpline(sketch, "E400", {"points": [v(198.1, 29.48) * mm, v(200.63, 35.58) * mm, v(202.81, 40.67) * mm, v(202.95, 40.8) * mm]});
            skFitSpline(sketch, "E401", {"points": [v(202.95, 40.8) * mm, v(203.09, 40.92) * mm, v(205, 41.26) * mm, v(207.2, 41.55) * mm]});
            skFitSpline(sketch, "E402", {"points": [v(207.2, 41.55) * mm, v(213.62, 42.4) * mm, v(213.78, 42.1) * mm, v(214.6, 27.2) * mm]});
            skFitSpline(sketch, "E403", {"points": [v(214.6, 27.2) * mm, v(214.98, 20.16) * mm, v(215.15, 13.95) * mm, v(214.96, 13.4) * mm]});
            skFitSpline(sketch, "E404", {"points": [v(214.96, 13.4) * mm, v(214.76, 12.78) * mm, v(213.13, 12.4) * mm, v(210.7, 12.4) * mm]});
            skFitSpline(sketch, "E405", {"points": [v(210.7, 12.4) * mm, v(207.23, 12.4) * mm, v(206.67, 12.64) * mm, v(206, 14.4) * mm]});
            skFitSpline(sketch, "E406", {"points": [v(206, 14.4) * mm, v(205.04, 16.92) * mm, v(202.39, 17.03) * mm, v(201.1, 14.6) * mm]});
            skFitSpline(sketch, "E407", {"points": [v(201.1, 14.6) * mm, v(200.59, 13.61) * mm, v(199.8, 12.56) * mm, v(199.35, 12.27) * mm]});
            skFitSpline(sketch, "E408", {"points": [v(199.35, 12.27) * mm, v(198.9, 11.98) * mm, v(193.01, 11.71) * mm, v(186.25, 11.67) * mm]});
            skFitSpline(sketch, "E409", {"points": [v(186.25, 11.67) * mm, v(176.52, 11.6) * mm, v(173.87, 11.82) * mm, v(173.53, 12.68) * mm]});
            skFitSpline(sketch, "E410", {"points": [v(205.99, 25.8) * mm, v(205.98, 27.51) * mm, v(205.8, 27.74) * mm, v(205.2, 26.8) * mm]});
            skFitSpline(sketch, "E411", {"points": [v(205.2, 26.8) * mm, v(204.19, 25.23) * mm, v(204.19, 23.6) * mm, v(205.2, 23.6) * mm]});
            skFitSpline(sketch, "E412", {"points": [v(205.2, 23.6) * mm, v(205.64, 23.6) * mm, v(206, 24.6) * mm, v(205.99, 25.8) * mm]});
            skFitSpline(sketch, "E413", {"points": [v(-35.99, 40.37) * mm, v(-37.53, 43.37) * mm, v(-37.04, 44.4) * mm, v(-34.05, 44.4) * mm]});
            skFitSpline(sketch, "E414", {"points": [v(-34.05, 44.4) * mm, v(-29.63, 44.4) * mm, v(-28.25, 38.65) * mm, v(-32.55, 38.15) * mm]});
            skFitSpline(sketch, "E415", {"points": [v(-32.55, 38.15) * mm, v(-34.28, 37.95) * mm, v(-34.97, 38.4) * mm, v(-35.99, 40.37) * mm]});
            skLineSegment(sketch, "E416.bottom", {"start": v(228.76, 97.57) * mm, "end": v(-164.39, 97.57) * mm});
            skLineSegment(sketch, "E416.top", {"start": v(228.76, -85.75) * mm, "end": v(-164.39, -85.75) * mm});
            skLineSegment(sketch, "E416.left", {"start": v(228.76, 97.57) * mm, "end": v(228.76, -85.75) * mm});
            skLineSegment(sketch, "E416.right", {"start": v(-164.39, 97.57) * mm, "end": v(-164.39, -85.75) * mm});
            skSolve(sketch);
        }
        {
            var Q0;
            Q0 = qSketchRegion(id + "F2", true);
            extrude(context, id + "F4", {"entities" : qUnion([Q0]), "depth" : 3.6 * mm});
        }
        {
            var Q0;
            Q0 = qSketchRegion(id + "F1", true);
            extrude(context, id + "F5", {"entities" : qUnion([Q0]), "operationType" : NewBodyOperationType.REMOVE, "depth" : 10 * mm, "hasSecondDirection" : true, "secondDirectionOppositeDirection" : true, "secondDirectionDepth" : 10 * mm});
        }
        {
            var Q0;
            Q0=makeQuery(id+"F4.opExtrude","SWEPT_BODY",BODY,{"disambiguationData":[OSD([sQuery(id+"F2.wireOp",EDGE,"E219.0"),sQuery(id+"F2.wireOp",EDGE,"E219.2"),sQuery(id+"F2.wireOp",EDGE,"E219.3"),sQuery(id+"F2.wireOp",EDGE,"E219.4"),sQuery(id+"F2.wireOp",EDGE,"E219.5"),sQuery(id+"F2.wireOp",EDGE,"E219.6"),sQuery(id+"F2.wireOp",EDGE,"E219.7"),sQuery(id+"F2.wireOp",EDGE,"E219.8"),sQuery(id+"F2.wireOp",EDGE,"E219.9"),sQuery(id+"F2.wireOp",EDGE,"E219.10"),sQuery(id+"F2.wireOp",EDGE,"E219.11"),sQuery(id+"F2.wireOp",EDGE,"E219.12"),sQuery(id+"F2.wireOp",EDGE,"E219.13"),sQuery(id+"F2.wireOp",EDGE,"E219.14"),sQuery(id+"F2.wireOp",EDGE,"E219.15"),sQuery(id+"F2.wireOp",EDGE,"E219.16"),sQuery(id+"F2.wireOp",EDGE,"E219.17"),sQuery(id+"F2.wireOp",EDGE,"E219.18"),sQuery(id+"F2.wireOp",EDGE,"E219.19"),sQuery(id+"F2.wireOp",EDGE,"E219.20"),sQuery(id+"F2.wireOp",EDGE,"E219.21"),sQuery(id+"F2.wireOp",EDGE,"E219.22"),sQuery(id+"F2.wireOp",EDGE,"E219.23"),sQuery(id+"F2.wireOp",EDGE,"E219.24"),sQuery(id+"F2.wireOp",EDGE,"E219.25"),sQuery(id+"F2.wireOp",EDGE,"E219.26"),sQuery(id+"F2.wireOp",EDGE,"E219.27"),sQuery(id+"F2.wireOp",EDGE,"E219.28"),sQuery(id+"F2.wireOp",EDGE,"E219.29"),sQuery(id+"F2.wireOp",EDGE,"E219.30"),sQuery(id+"F2.wireOp",EDGE,"E219.33"),sQuery(id+"F2.wireOp",EDGE,"E219.34"),sQuery(id+"F2.wireOp",EDGE,"E219.35"),sQuery(id+"F2.wireOp",EDGE,"E219.36"),sQuery(id+"F2.wireOp",EDGE,"E219.37"),sQuery(id+"F2.wireOp",EDGE,"E219.39"),sQuery(id+"F2.wireOp",EDGE,"E219.40"),sQuery(id+"F2.wireOp",EDGE,"E219.41"),sQuery(id+"F2.wireOp",EDGE,"E219.42"),sQuery(id+"F2.wireOp",EDGE,"E219.43"),sQuery(id+"F2.wireOp",EDGE,"E219.44"),sQuery(id+"F2.wireOp",EDGE,"E219.45"),sQuery(id+"F2.wireOp",EDGE,"E219.46"),sQuery(id+"F2.wireOp",EDGE,"E219.47"),sQuery(id+"F2.wireOp",EDGE,"E219.48"),sQuery(id+"F2.wireOp",EDGE,"E219.49"),sQuery(id+"F2.wireOp",EDGE,"E219.50"),sQuery(id+"F2.wireOp",EDGE,"E219.51"),sQuery(id+"F2.wireOp",EDGE,"E219.52"),sQuery(id+"F2.wireOp",EDGE,"E219.53"),sQuery(id+"F2.wireOp",EDGE,"E219.54"),sQuery(id+"F2.wireOp",EDGE,"E219.55"),sQuery(id+"F2.wireOp",EDGE,"E219.56"),sQuery(id+"F2.wireOp",EDGE,"E219.57"),sQuery(id+"F2.wireOp",EDGE,"E219.58"),sQuery(id+"F2.wireOp",EDGE,"E219.59"),sQuery(id+"F2.wireOp",EDGE,"E219.60"),sQuery(id+"F2.wireOp",EDGE,"E219.61"),sQuery(id+"F2.wireOp",EDGE,"E219.62"),sQuery(id+"F2.wireOp",EDGE,"E219.63"),sQuery(id+"F2.wireOp",EDGE,"E219.64"),sQuery(id+"F2.wireOp",EDGE,"E219.65"),sQuery(id+"F2.wireOp",EDGE,"E219.66"),sQuery(id+"F2.wireOp",EDGE,"E219.67"),sQuery(id+"F2.wireOp",EDGE,"E219.68"),sQuery(id+"F2.wireOp",EDGE,"E219.69")])]});
            var Q1;
            Q1=makeQuery(id+"F5.opExtrude","SWEPT_BODY",BODY,{"disambiguationData":[OSD([sQuery(id+"F1.wireOp",EDGE,"E218.0.0"),sQuery(id+"F1.wireOp",EDGE,"E218.0.1"),sQuery(id+"F1.wireOp",EDGE,"E218.0.2"),sQuery(id+"F1.wireOp",EDGE,"E218.0.3"),sQuery(id+"F1.wireOp",EDGE,"E218.0.4"),sQuery(id+"F1.wireOp",EDGE,"E218.0.5"),sQuery(id+"F1.wireOp",EDGE,"E218.0.6"),sQuery(id+"F1.wireOp",EDGE,"E218.0.7"),sQuery(id+"F1.wireOp",EDGE,"E218.0.8"),sQuery(id+"F1.wireOp",EDGE,"E218.0.9"),sQuery(id+"F1.wireOp",EDGE,"E218.0.10"),sQuery(id+"F1.wireOp",EDGE,"E218.0.11"),sQuery(id+"F1.wireOp",EDGE,"E218.0.12"),sQuery(id+"F1.wireOp",EDGE,"E218.0.13"),sQuery(id+"F1.wireOp",EDGE,"E218.0.14"),sQuery(id+"F1.wireOp",EDGE,"E218.0.15"),sQuery(id+"F1.wireOp",EDGE,"E218.0.16"),sQuery(id+"F1.wireOp",EDGE,"E218.0.17"),sQuery(id+"F1.wireOp",EDGE,"E218.0.18"),sQuery(id+"F1.wireOp",EDGE,"E218.0.19"),sQuery(id+"F1.wireOp",EDGE,"E218.0.20"),sQuery(id+"F1.wireOp",EDGE,"E218.0.21"),sQuery(id+"F1.wireOp",EDGE,"E218.0.22"),sQuery(id+"F1.wireOp",EDGE,"E218.0.23"),sQuery(id+"F1.wireOp",EDGE,"E218.0.24"),sQuery(id+"F1.wireOp",EDGE,"E218.0.25"),sQuery(id+"F1.wireOp",EDGE,"E218.0.26"),sQuery(id+"F1.wireOp",EDGE,"E218.0.27"),sQuery(id+"F1.wireOp",EDGE,"E218.0.28"),sQuery(id+"F1.wireOp",EDGE,"E218.0.29"),sQuery(id+"F1.wireOp",EDGE,"E218.0.30"),sQuery(id+"F1.wireOp",EDGE,"E218.0.31"),sQuery(id+"F1.wireOp",EDGE,"E218.0.32"),sQuery(id+"F1.wireOp",EDGE,"E218.0.33"),sQuery(id+"F1.wireOp",EDGE,"E218.0.36"),sQuery(id+"F1.wireOp",EDGE,"E218.0.37"),sQuery(id+"F1.wireOp",EDGE,"E218.0.38"),sQuery(id+"F1.wireOp",EDGE,"E218.0.39"),sQuery(id+"F1.wireOp",EDGE,"E218.0.40"),sQuery(id+"F1.wireOp",EDGE,"E218.0.41"),sQuery(id+"F1.wireOp",EDGE,"E218.0.42"),sQuery(id+"F1.wireOp",EDGE,"E218.0.43"),sQuery(id+"F1.wireOp",EDGE,"E218.0.44"),sQuery(id+"F1.wireOp",EDGE,"E218.0.45"),sQuery(id+"F1.wireOp",EDGE,"E218.0.46"),sQuery(id+"F1.wireOp",EDGE,"E218.0.47"),sQuery(id+"F1.wireOp",EDGE,"E218.0.48"),sQuery(id+"F1.wireOp",EDGE,"E218.0.49"),sQuery(id+"F1.wireOp",EDGE,"E218.0.50"),sQuery(id+"F1.wireOp",EDGE,"E218.0.51"),sQuery(id+"F1.wireOp",EDGE,"E218.0.52"),sQuery(id+"F1.wireOp",EDGE,"E218.0.53"),sQuery(id+"F1.wireOp",EDGE,"E218.0.54"),sQuery(id+"F1.wireOp",EDGE,"E218.0.55"),sQuery(id+"F1.wireOp",EDGE,"E218.0.56"),sQuery(id+"F1.wireOp",EDGE,"E218.0.57"),sQuery(id+"F1.wireOp",EDGE,"E218.0.58"),sQuery(id+"F1.wireOp",EDGE,"E218.0.59"),sQuery(id+"F1.wireOp",EDGE,"E218.0.60"),sQuery(id+"F1.wireOp",EDGE,"E218.0.61"),sQuery(id+"F1.wireOp",EDGE,"E218.0.62"),sQuery(id+"F1.wireOp",EDGE,"E218.0.63"),sQuery(id+"F1.wireOp",EDGE,"E218.0.64"),sQuery(id+"F1.wireOp",EDGE,"E218.0.65"),sQuery(id+"F1.wireOp",EDGE,"E218.0.66"),sQuery(id+"F1.wireOp",EDGE,"E218.0.67"),sQuery(id+"F1.wireOp",EDGE,"E218.0.68"),sQuery(id+"F1.wireOp",EDGE,"E218.0.69"),sQuery(id+"F1.wireOp",EDGE,"E218.0.70"),sQuery(id+"F1.wireOp",EDGE,"E218.0.71"),sQuery(id+"F1.wireOp",EDGE,"E218.0.72"),sQuery(id+"F1.wireOp",EDGE,"E218.0.73"),sQuery(id+"F1.wireOp",EDGE,"E218.0.74"),sQuery(id+"F1.wireOp",EDGE,"E218.0.75"),sQuery(id+"F1.wireOp",EDGE,"E218.0.76"),sQuery(id+"F1.wireOp",EDGE,"E218.0.77"),sQuery(id+"F1.wireOp",EDGE,"E218.0.78"),sQuery(id+"F1.wireOp",EDGE,"E218.0.79"),sQuery(id+"F1.wireOp",EDGE,"E218.0.80"),sQuery(id+"F1.wireOp",EDGE,"E218.0.81"),sQuery(id+"F1.wireOp",EDGE,"E218.0.82"),sQuery(id+"F1.wireOp",EDGE,"E218.0.83"),sQuery(id+"F1.wireOp",EDGE,"E218.0.84"),sQuery(id+"F1.wireOp",EDGE,"E218.0.85"),sQuery(id+"F1.wireOp",EDGE,"E218.0.86"),sQuery(id+"F1.wireOp",EDGE,"E218.0.87"),sQuery(id+"F1.wireOp",EDGE,"E218.0.88"),sQuery(id+"F1.wireOp",EDGE,"E218.0.89"),sQuery(id+"F1.wireOp",EDGE,"E218.0.90"),sQuery(id+"F1.wireOp",EDGE,"E218.0.91"),sQuery(id+"F1.wireOp",EDGE,"E218.0.92"),sQuery(id+"F1.wireOp",EDGE,"E218.0.93"),sQuery(id+"F1.wireOp",EDGE,"E218.0.94")])]});
            var Q2;
            Q2=makeQuery(id+"F5.opExtrude","SWEPT_BODY",BODY,{"disambiguationData":[OSD([sQuery(id+"F1.wireOp",EDGE,"E218.1.0"),sQuery(id+"F1.wireOp",EDGE,"E218.1.1"),sQuery(id+"F1.wireOp",EDGE,"E218.1.2"),sQuery(id+"F1.wireOp",EDGE,"E218.1.3"),sQuery(id+"F1.wireOp",EDGE,"E218.1.4"),sQuery(id+"F1.wireOp",EDGE,"E218.1.5"),sQuery(id+"F1.wireOp",EDGE,"E218.1.6"),sQuery(id+"F1.wireOp",EDGE,"E218.1.7"),sQuery(id+"F1.wireOp",EDGE,"E218.1.8"),sQuery(id+"F1.wireOp",EDGE,"E218.1.9"),sQuery(id+"F1.wireOp",EDGE,"E218.1.10"),sQuery(id+"F1.wireOp",EDGE,"E218.1.11"),sQuery(id+"F1.wireOp",EDGE,"E218.1.12"),sQuery(id+"F1.wireOp",EDGE,"E218.1.13"),sQuery(id+"F1.wireOp",EDGE,"E218.1.14"),sQuery(id+"F1.wireOp",EDGE,"E218.1.15"),sQuery(id+"F1.wireOp",EDGE,"E218.1.16"),sQuery(id+"F1.wireOp",EDGE,"E218.1.17"),sQuery(id+"F1.wireOp",EDGE,"E218.1.18"),sQuery(id+"F1.wireOp",EDGE,"E218.1.19"),sQuery(id+"F1.wireOp",EDGE,"E218.1.20"),sQuery(id+"F1.wireOp",EDGE,"E218.1.21"),sQuery(id+"F1.wireOp",EDGE,"E218.1.22"),sQuery(id+"F1.wireOp",EDGE,"E218.1.23"),sQuery(id+"F1.wireOp",EDGE,"E218.1.24"),sQuery(id+"F1.wireOp",EDGE,"E218.1.25"),sQuery(id+"F1.wireOp",EDGE,"E218.1.26"),sQuery(id+"F1.wireOp",EDGE,"E218.1.27"),sQuery(id+"F1.wireOp",EDGE,"E218.1.28"),sQuery(id+"F1.wireOp",EDGE,"E218.1.29"),sQuery(id+"F1.wireOp",EDGE,"E218.1.30"),sQuery(id+"F1.wireOp",EDGE,"E218.1.31"),sQuery(id+"F1.wireOp",EDGE,"E218.1.32"),sQuery(id+"F1.wireOp",EDGE,"E218.1.33"),sQuery(id+"F1.wireOp",EDGE,"E218.1.34"),sQuery(id+"F1.wireOp",EDGE,"E218.1.35"),sQuery(id+"F1.wireOp",EDGE,"E218.1.36"),sQuery(id+"F1.wireOp",EDGE,"E218.1.37"),sQuery(id+"F1.wireOp",EDGE,"E218.1.38"),sQuery(id+"F1.wireOp",EDGE,"E218.1.39"),sQuery(id+"F1.wireOp",EDGE,"E218.1.40"),sQuery(id+"F1.wireOp",EDGE,"E218.1.41"),sQuery(id+"F1.wireOp",EDGE,"E218.1.42"),sQuery(id+"F1.wireOp",EDGE,"E218.1.43"),sQuery(id+"F1.wireOp",EDGE,"E218.1.44"),sQuery(id+"F1.wireOp",EDGE,"E218.1.45"),sQuery(id+"F1.wireOp",EDGE,"E218.1.46"),sQuery(id+"F1.wireOp",EDGE,"E218.1.47"),sQuery(id+"F1.wireOp",EDGE,"E218.1.48"),sQuery(id+"F1.wireOp",EDGE,"E218.1.49"),sQuery(id+"F1.wireOp",EDGE,"E218.1.50"),sQuery(id+"F1.wireOp",EDGE,"E218.1.51"),sQuery(id+"F1.wireOp",EDGE,"E218.1.52"),sQuery(id+"F1.wireOp",EDGE,"E218.1.53"),sQuery(id+"F1.wireOp",EDGE,"E218.1.54"),sQuery(id+"F1.wireOp",EDGE,"E218.1.55")])]});
            var Q3;
            Q3=makeQuery(id+"F4.opExtrude","CAP_VERTEX",VERTEX,{"disambiguationData":[OSD([sQuery(id+"F2.wireOp",EDGE,"E219.66"),sQuery(id+"F2.wireOp",EDGE,"E219.67")])],"isStart":true});
            transform(context, id + "F6", {"entities" : qUnion([Q0, Q1, Q2]), "transformType" : TransformType.SCALE_UNIFORMLY, "scale" : 0.6, "scalePoint" : qUnion([Q3]), "makeCopy" : false});
        }
        {
            var Q0;
            Q0=makeQuery(id+"F4.opExtrude","SWEPT_BODY",BODY,{"disambiguationData":[OSD([sQuery(id+"F2.wireOp",EDGE,"E219.0"),sQuery(id+"F2.wireOp",EDGE,"E219.2"),sQuery(id+"F2.wireOp",EDGE,"E219.3"),sQuery(id+"F2.wireOp",EDGE,"E219.4"),sQuery(id+"F2.wireOp",EDGE,"E219.5"),sQuery(id+"F2.wireOp",EDGE,"E219.6"),sQuery(id+"F2.wireOp",EDGE,"E219.7"),sQuery(id+"F2.wireOp",EDGE,"E219.8"),sQuery(id+"F2.wireOp",EDGE,"E219.9"),sQuery(id+"F2.wireOp",EDGE,"E219.10"),sQuery(id+"F2.wireOp",EDGE,"E219.11"),sQuery(id+"F2.wireOp",EDGE,"E219.12"),sQuery(id+"F2.wireOp",EDGE,"E219.13"),sQuery(id+"F2.wireOp",EDGE,"E219.14"),sQuery(id+"F2.wireOp",EDGE,"E219.15"),sQuery(id+"F2.wireOp",EDGE,"E219.16"),sQuery(id+"F2.wireOp",EDGE,"E219.17"),sQuery(id+"F2.wireOp",EDGE,"E219.18"),sQuery(id+"F2.wireOp",EDGE,"E219.19"),sQuery(id+"F2.wireOp",EDGE,"E219.20"),sQuery(id+"F2.wireOp",EDGE,"E219.21"),sQuery(id+"F2.wireOp",EDGE,"E219.22"),sQuery(id+"F2.wireOp",EDGE,"E219.23"),sQuery(id+"F2.wireOp",EDGE,"E219.24"),sQuery(id+"F2.wireOp",EDGE,"E219.25"),sQuery(id+"F2.wireOp",EDGE,"E219.26"),sQuery(id+"F2.wireOp",EDGE,"E219.27"),sQuery(id+"F2.wireOp",EDGE,"E219.28"),sQuery(id+"F2.wireOp",EDGE,"E219.29"),sQuery(id+"F2.wireOp",EDGE,"E219.30"),sQuery(id+"F2.wireOp",EDGE,"E219.33"),sQuery(id+"F2.wireOp",EDGE,"E219.34"),sQuery(id+"F2.wireOp",EDGE,"E219.35"),sQuery(id+"F2.wireOp",EDGE,"E219.36"),sQuery(id+"F2.wireOp",EDGE,"E219.37"),sQuery(id+"F2.wireOp",EDGE,"E219.39"),sQuery(id+"F2.wireOp",EDGE,"E219.40"),sQuery(id+"F2.wireOp",EDGE,"E219.41"),sQuery(id+"F2.wireOp",EDGE,"E219.42"),sQuery(id+"F2.wireOp",EDGE,"E219.43"),sQuery(id+"F2.wireOp",EDGE,"E219.44"),sQuery(id+"F2.wireOp",EDGE,"E219.45"),sQuery(id+"F2.wireOp",EDGE,"E219.46"),sQuery(id+"F2.wireOp",EDGE,"E219.47"),sQuery(id+"F2.wireOp",EDGE,"E219.48"),sQuery(id+"F2.wireOp",EDGE,"E219.49"),sQuery(id+"F2.wireOp",EDGE,"E219.50"),sQuery(id+"F2.wireOp",EDGE,"E219.51"),sQuery(id+"F2.wireOp",EDGE,"E219.52"),sQuery(id+"F2.wireOp",EDGE,"E219.53"),sQuery(id+"F2.wireOp",EDGE,"E219.54"),sQuery(id+"F2.wireOp",EDGE,"E219.55"),sQuery(id+"F2.wireOp",EDGE,"E219.56"),sQuery(id+"F2.wireOp",EDGE,"E219.57"),sQuery(id+"F2.wireOp",EDGE,"E219.58"),sQuery(id+"F2.wireOp",EDGE,"E219.59"),sQuery(id+"F2.wireOp",EDGE,"E219.60"),sQuery(id+"F2.wireOp",EDGE,"E219.61"),sQuery(id+"F2.wireOp",EDGE,"E219.62"),sQuery(id+"F2.wireOp",EDGE,"E219.63"),sQuery(id+"F2.wireOp",EDGE,"E219.64"),sQuery(id+"F2.wireOp",EDGE,"E219.65"),sQuery(id+"F2.wireOp",EDGE,"E219.66"),sQuery(id+"F2.wireOp",EDGE,"E219.67"),sQuery(id+"F2.wireOp",EDGE,"E219.68"),sQuery(id+"F2.wireOp",EDGE,"E219.69")])]});
            var Q1;
            Q1=makeQuery(id+"F5.opExtrude","SWEPT_BODY",BODY,{"disambiguationData":[OSD([sQuery(id+"F1.wireOp",EDGE,"E218.1.0"),sQuery(id+"F1.wireOp",EDGE,"E218.1.1"),sQuery(id+"F1.wireOp",EDGE,"E218.1.2"),sQuery(id+"F1.wireOp",EDGE,"E218.1.3"),sQuery(id+"F1.wireOp",EDGE,"E218.1.4"),sQuery(id+"F1.wireOp",EDGE,"E218.1.5"),sQuery(id+"F1.wireOp",EDGE,"E218.1.6"),sQuery(id+"F1.wireOp",EDGE,"E218.1.7"),sQuery(id+"F1.wireOp",EDGE,"E218.1.8"),sQuery(id+"F1.wireOp",EDGE,"E218.1.9"),sQuery(id+"F1.wireOp",EDGE,"E218.1.10"),sQuery(id+"F1.wireOp",EDGE,"E218.1.11"),sQuery(id+"F1.wireOp",EDGE,"E218.1.12"),sQuery(id+"F1.wireOp",EDGE,"E218.1.13"),sQuery(id+"F1.wireOp",EDGE,"E218.1.14"),sQuery(id+"F1.wireOp",EDGE,"E218.1.15"),sQuery(id+"F1.wireOp",EDGE,"E218.1.16"),sQuery(id+"F1.wireOp",EDGE,"E218.1.17"),sQuery(id+"F1.wireOp",EDGE,"E218.1.18"),sQuery(id+"F1.wireOp",EDGE,"E218.1.19"),sQuery(id+"F1.wireOp",EDGE,"E218.1.20"),sQuery(id+"F1.wireOp",EDGE,"E218.1.21"),sQuery(id+"F1.wireOp",EDGE,"E218.1.22"),sQuery(id+"F1.wireOp",EDGE,"E218.1.23"),sQuery(id+"F1.wireOp",EDGE,"E218.1.24"),sQuery(id+"F1.wireOp",EDGE,"E218.1.25"),sQuery(id+"F1.wireOp",EDGE,"E218.1.26"),sQuery(id+"F1.wireOp",EDGE,"E218.1.27"),sQuery(id+"F1.wireOp",EDGE,"E218.1.28"),sQuery(id+"F1.wireOp",EDGE,"E218.1.29"),sQuery(id+"F1.wireOp",EDGE,"E218.1.30"),sQuery(id+"F1.wireOp",EDGE,"E218.1.31"),sQuery(id+"F1.wireOp",EDGE,"E218.1.32"),sQuery(id+"F1.wireOp",EDGE,"E218.1.33"),sQuery(id+"F1.wireOp",EDGE,"E218.1.34"),sQuery(id+"F1.wireOp",EDGE,"E218.1.35"),sQuery(id+"F1.wireOp",EDGE,"E218.1.36"),sQuery(id+"F1.wireOp",EDGE,"E218.1.37"),sQuery(id+"F1.wireOp",EDGE,"E218.1.38"),sQuery(id+"F1.wireOp",EDGE,"E218.1.39"),sQuery(id+"F1.wireOp",EDGE,"E218.1.40"),sQuery(id+"F1.wireOp",EDGE,"E218.1.41"),sQuery(id+"F1.wireOp",EDGE,"E218.1.42"),sQuery(id+"F1.wireOp",EDGE,"E218.1.43"),sQuery(id+"F1.wireOp",EDGE,"E218.1.44"),sQuery(id+"F1.wireOp",EDGE,"E218.1.45"),sQuery(id+"F1.wireOp",EDGE,"E218.1.46"),sQuery(id+"F1.wireOp",EDGE,"E218.1.47"),sQuery(id+"F1.wireOp",EDGE,"E218.1.48"),sQuery(id+"F1.wireOp",EDGE,"E218.1.49"),sQuery(id+"F1.wireOp",EDGE,"E218.1.50"),sQuery(id+"F1.wireOp",EDGE,"E218.1.51"),sQuery(id+"F1.wireOp",EDGE,"E218.1.52"),sQuery(id+"F1.wireOp",EDGE,"E218.1.53"),sQuery(id+"F1.wireOp",EDGE,"E218.1.54"),sQuery(id+"F1.wireOp",EDGE,"E218.1.55")])]});
            var Q2;
            Q2=makeQuery(id+"F5.opExtrude","SWEPT_BODY",BODY,{"disambiguationData":[OSD([sQuery(id+"F1.wireOp",EDGE,"E218.0.0"),sQuery(id+"F1.wireOp",EDGE,"E218.0.1"),sQuery(id+"F1.wireOp",EDGE,"E218.0.2"),sQuery(id+"F1.wireOp",EDGE,"E218.0.3"),sQuery(id+"F1.wireOp",EDGE,"E218.0.4"),sQuery(id+"F1.wireOp",EDGE,"E218.0.5"),sQuery(id+"F1.wireOp",EDGE,"E218.0.6"),sQuery(id+"F1.wireOp",EDGE,"E218.0.7"),sQuery(id+"F1.wireOp",EDGE,"E218.0.8"),sQuery(id+"F1.wireOp",EDGE,"E218.0.9"),sQuery(id+"F1.wireOp",EDGE,"E218.0.10"),sQuery(id+"F1.wireOp",EDGE,"E218.0.11"),sQuery(id+"F1.wireOp",EDGE,"E218.0.12"),sQuery(id+"F1.wireOp",EDGE,"E218.0.13"),sQuery(id+"F1.wireOp",EDGE,"E218.0.14"),sQuery(id+"F1.wireOp",EDGE,"E218.0.15"),sQuery(id+"F1.wireOp",EDGE,"E218.0.16"),sQuery(id+"F1.wireOp",EDGE,"E218.0.17"),sQuery(id+"F1.wireOp",EDGE,"E218.0.18"),sQuery(id+"F1.wireOp",EDGE,"E218.0.19"),sQuery(id+"F1.wireOp",EDGE,"E218.0.20"),sQuery(id+"F1.wireOp",EDGE,"E218.0.21"),sQuery(id+"F1.wireOp",EDGE,"E218.0.22"),sQuery(id+"F1.wireOp",EDGE,"E218.0.23"),sQuery(id+"F1.wireOp",EDGE,"E218.0.24"),sQuery(id+"F1.wireOp",EDGE,"E218.0.25"),sQuery(id+"F1.wireOp",EDGE,"E218.0.26"),sQuery(id+"F1.wireOp",EDGE,"E218.0.27"),sQuery(id+"F1.wireOp",EDGE,"E218.0.28"),sQuery(id+"F1.wireOp",EDGE,"E218.0.29"),sQuery(id+"F1.wireOp",EDGE,"E218.0.30"),sQuery(id+"F1.wireOp",EDGE,"E218.0.31"),sQuery(id+"F1.wireOp",EDGE,"E218.0.32"),sQuery(id+"F1.wireOp",EDGE,"E218.0.33"),sQuery(id+"F1.wireOp",EDGE,"E218.0.36"),sQuery(id+"F1.wireOp",EDGE,"E218.0.37"),sQuery(id+"F1.wireOp",EDGE,"E218.0.38"),sQuery(id+"F1.wireOp",EDGE,"E218.0.39"),sQuery(id+"F1.wireOp",EDGE,"E218.0.40"),sQuery(id+"F1.wireOp",EDGE,"E218.0.41"),sQuery(id+"F1.wireOp",EDGE,"E218.0.42"),sQuery(id+"F1.wireOp",EDGE,"E218.0.43"),sQuery(id+"F1.wireOp",EDGE,"E218.0.44"),sQuery(id+"F1.wireOp",EDGE,"E218.0.45"),sQuery(id+"F1.wireOp",EDGE,"E218.0.46"),sQuery(id+"F1.wireOp",EDGE,"E218.0.47"),sQuery(id+"F1.wireOp",EDGE,"E218.0.48"),sQuery(id+"F1.wireOp",EDGE,"E218.0.49"),sQuery(id+"F1.wireOp",EDGE,"E218.0.50"),sQuery(id+"F1.wireOp",EDGE,"E218.0.51"),sQuery(id+"F1.wireOp",EDGE,"E218.0.52"),sQuery(id+"F1.wireOp",EDGE,"E218.0.53"),sQuery(id+"F1.wireOp",EDGE,"E218.0.54"),sQuery(id+"F1.wireOp",EDGE,"E218.0.55"),sQuery(id+"F1.wireOp",EDGE,"E218.0.56"),sQuery(id+"F1.wireOp",EDGE,"E218.0.57"),sQuery(id+"F1.wireOp",EDGE,"E218.0.58"),sQuery(id+"F1.wireOp",EDGE,"E218.0.59"),sQuery(id+"F1.wireOp",EDGE,"E218.0.60"),sQuery(id+"F1.wireOp",EDGE,"E218.0.61"),sQuery(id+"F1.wireOp",EDGE,"E218.0.62"),sQuery(id+"F1.wireOp",EDGE,"E218.0.63"),sQuery(id+"F1.wireOp",EDGE,"E218.0.64"),sQuery(id+"F1.wireOp",EDGE,"E218.0.65"),sQuery(id+"F1.wireOp",EDGE,"E218.0.66"),sQuery(id+"F1.wireOp",EDGE,"E218.0.67"),sQuery(id+"F1.wireOp",EDGE,"E218.0.68"),sQuery(id+"F1.wireOp",EDGE,"E218.0.69"),sQuery(id+"F1.wireOp",EDGE,"E218.0.70"),sQuery(id+"F1.wireOp",EDGE,"E218.0.71"),sQuery(id+"F1.wireOp",EDGE,"E218.0.72"),sQuery(id+"F1.wireOp",EDGE,"E218.0.73"),sQuery(id+"F1.wireOp",EDGE,"E218.0.74"),sQuery(id+"F1.wireOp",EDGE,"E218.0.75"),sQuery(id+"F1.wireOp",EDGE,"E218.0.76"),sQuery(id+"F1.wireOp",EDGE,"E218.0.77"),sQuery(id+"F1.wireOp",EDGE,"E218.0.78"),sQuery(id+"F1.wireOp",EDGE,"E218.0.79"),sQuery(id+"F1.wireOp",EDGE,"E218.0.80"),sQuery(id+"F1.wireOp",EDGE,"E218.0.81"),sQuery(id+"F1.wireOp",EDGE,"E218.0.82"),sQuery(id+"F1.wireOp",EDGE,"E218.0.83"),sQuery(id+"F1.wireOp",EDGE,"E218.0.84"),sQuery(id+"F1.wireOp",EDGE,"E218.0.85"),sQuery(id+"F1.wireOp",EDGE,"E218.0.86"),sQuery(id+"F1.wireOp",EDGE,"E218.0.87"),sQuery(id+"F1.wireOp",EDGE,"E218.0.88"),sQuery(id+"F1.wireOp",EDGE,"E218.0.89"),sQuery(id+"F1.wireOp",EDGE,"E218.0.90"),sQuery(id+"F1.wireOp",EDGE,"E218.0.91"),sQuery(id+"F1.wireOp",EDGE,"E218.0.92"),sQuery(id+"F1.wireOp",EDGE,"E218.0.93"),sQuery(id+"F1.wireOp",EDGE,"E218.0.94")])]});
            transform(context, id + "F7", {"entities" : qUnion([Q0, Q1, Q2]), "transformType" : TransformType.TRANSLATION_3D, "dx" : 69.8 * mm, "dy" : 53.1 * mm, "dz" : 0 * mm, "makeCopy" : false});
        }
        {
            var Q0;
            Q0=makeQuery(id+"F3.imprint","IMPRINT",FACE,{"disambiguationData":[TD([[makeQuery(id+"F3.imprint","IMPRINT",EDGE,{"derivedFrom":sQuery(id+"F3.wireOp",EDGE,"E220")}),1.0]])]});
            var Q1;
            Q1=makeQuery(id+"F3.imprint","IMPRINT",FACE,{"disambiguationData":[TD([[makeQuery(id+"F3.imprint","IMPRINT",EDGE,{"derivedFrom":sQuery(id+"F3.wireOp",EDGE,"E380")}),1.0]])]});
            var Q2;
            Q2=makeQuery(id+"F3.imprint","IMPRINT",FACE,{"disambiguationData":[TD([[makeQuery(id+"F3.imprint","IMPRINT",EDGE,{"derivedFrom":sQuery(id+"F3.wireOp",EDGE,"E410")}),1.0]])]});
            var Q3;
            Q3=makeQuery(id+"F3.imprint","IMPRINT",FACE,{"disambiguationData":[TD([[makeQuery(id+"F3.imprint","IMPRINT",EDGE,{"derivedFrom":sQuery(id+"F3.wireOp",EDGE,"E300")}),1.0]])]});
            var Q4;
            Q4=makeQuery(id+"F3.imprint","IMPRINT",FACE,{"disambiguationData":[TD([[makeQuery(id+"F3.imprint","IMPRINT",EDGE,{"derivedFrom":sQuery(id+"F3.wireOp",EDGE,"E281")}),1.0]])]});
            extrude(context, id + "F8", {"entities" : qUnion([Q0, Q1, Q2, Q3, Q4]), "operationType" : NewBodyOperationType.ADD, "oppositeDirection" : true, "depth" : 1.6 * mm});
        }
    });
